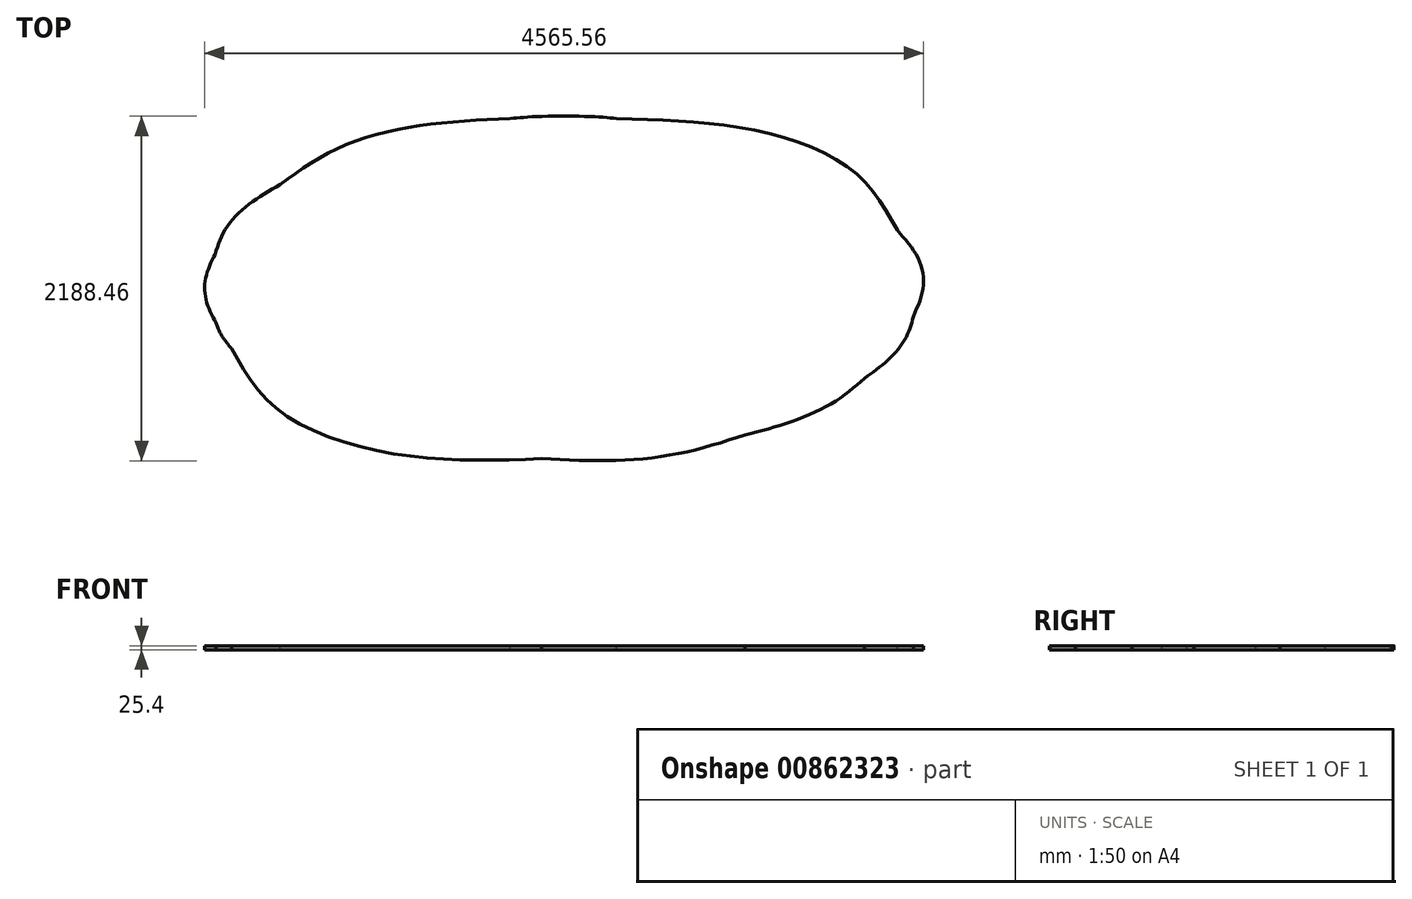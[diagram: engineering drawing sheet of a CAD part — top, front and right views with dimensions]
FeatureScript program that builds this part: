
annotation { "Feature Type Name" : "Feature", "Feature Type Description" : "" }
export const myFeature = defineFeature(function(context is Context, id is Id, definition is map)
    precondition{}
    {
        {
            var Q0;
            Q0=qCreatedBy(makeId("Top.planeOp"),FACE);
            var sketch = newSketch(context, id + "F0", { "sketchPlane" : qUnion([Q0])});
            skLineSegment(sketch, "E0", {"start": v(-77.13, -787.1) * mm, "end": v(-35, -787.1) * mm});
            skLineSegment(sketch, "E1", {"start": v(-35, -787.1) * mm, "end": v(-21.6, -746.82) * mm});
            skLineSegment(sketch, "E2", {"start": v(21.27, -746.77) * mm, "end": v(33.87, -784.57) * mm});
            skLineSegment(sketch, "E3", {"start": v(33.87, -784.57) * mm, "end": v(77.97, -786.03) * mm});
            skLineSegment(sketch, "E4", {"start": v(87.03, -826.55) * mm, "end": v(52.38, -853.41) * mm});
            skLineSegment(sketch, "E5", {"start": v(52.38, -853.41) * mm, "end": v(64.55, -889.18) * mm});
            skLineSegment(sketch, "E6", {"start": v(-79.54, -938.83) * mm, "end": v(-79.54, -938.83) * mm});
            skLineSegment(sketch, "E7", {"start": v(-405.14, -731.65) * mm, "end": v(-373.47, -731.65) * mm});
            skLineSegment(sketch, "E8", {"start": v(-373.47, -731.65) * mm, "end": v(-364.31, -701.4) * mm});
            skLineSegment(sketch, "E9", {"start": v(-330.23, -701.41) * mm, "end": v(-321.34, -731.65) * mm});
            skLineSegment(sketch, "E10", {"start": v(-321.34, -731.65) * mm, "end": v(-288.94, -731.65) * mm});
            skLineSegment(sketch, "E11", {"start": v(-288.47, -772.67) * mm, "end": v(-303.5, -785.97) * mm});
            skLineSegment(sketch, "E12", {"start": v(-303.5, -785.97) * mm, "end": v(-294.85, -813.44) * mm});
            skLineSegment(sketch, "E13", {"start": v(-322.06, -834.55) * mm, "end": v(-346.67, -816.48) * mm});
            skLineSegment(sketch, "E14", {"start": v(-346.67, -816.48) * mm, "end": v(-371.3, -834.55) * mm});
            skLineSegment(sketch, "E15", {"start": v(292.75, -813.28) * mm, "end": v(302.15, -783.08) * mm});
            skLineSegment(sketch, "E16", {"start": v(302.15, -783.08) * mm, "end": v(277.64, -764.38) * mm});
            skLineSegment(sketch, "E17", {"start": v(285.47, -731.65) * mm, "end": v(317.8, -731.65) * mm});
            skLineSegment(sketch, "E18", {"start": v(317.8, -731.65) * mm, "end": v(327.47, -702.67) * mm});
            skLineSegment(sketch, "E19", {"start": v(362.59, -701.06) * mm, "end": v(371.57, -731.64) * mm});
            skLineSegment(sketch, "E20", {"start": v(371.57, -731.64) * mm, "end": v(405.6, -731.64) * mm});
            skLineSegment(sketch, "E21", {"start": v(364.32, -830.54) * mm, "end": v(343.95, -816.03) * mm});
            skLineSegment(sketch, "E22", {"start": v(343.95, -816.03) * mm, "end": v(321.63, -834.33) * mm});
            skLineSegment(sketch, "E23", {"start": v(-1400.1, -366.23) * mm, "end": v(-1400.1, -398.99) * mm});
            skLineSegment(sketch, "E24", {"start": v(-1400.1, -398.99) * mm, "end": v(-1347.18, -398.99) * mm});
            skLineSegment(sketch, "E25", {"start": v(-1347.18, -398.99) * mm, "end": v(-1294.25, -398.99) * mm});
            skLineSegment(sketch, "E26", {"start": v(-1294.25, -398.99) * mm, "end": v(-1294.25, -369.56) * mm});
            skLineSegment(sketch, "E27", {"start": v(-1294.25, -458.02) * mm, "end": v(-1294.25, -429.23) * mm});
            skLineSegment(sketch, "E28", {"start": v(-1294.25, -429.23) * mm, "end": v(-1347.18, -429.23) * mm});
            skLineSegment(sketch, "E29", {"start": v(-1347.18, -429.23) * mm, "end": v(-1400.1, -429.23) * mm});
            skLineSegment(sketch, "E30", {"start": v(-1400.1, -429.23) * mm, "end": v(-1400.1, -461.65) * mm});
            skLineSegment(sketch, "E31", {"start": v(-1121.42, -405.3) * mm, "end": v(-1083.64, -310.78) * mm});
            skLineSegment(sketch, "E32", {"start": v(-1083.64, -310.78) * mm, "end": v(-1062.94, -309.23) * mm});
            skLineSegment(sketch, "E33", {"start": v(-1063.2, -465.59) * mm, "end": v(-1106.64, -464.14) * mm});
            skLineSegment(sketch, "E34", {"start": v(-1106.64, -464.14) * mm, "end": v(-1111.77, -478.84) * mm});
            skLineSegment(sketch, "E35", {"start": v(-823.63, -524) * mm, "end": v(-839.34, -525.54) * mm});
            skLineSegment(sketch, "E36", {"start": v(-839.34, -525.54) * mm, "end": v(-875.93, -434.22) * mm});
            skLineSegment(sketch, "E37", {"start": v(-571.43, -308.26) * mm, "end": v(-493.78, -308.26) * mm});
            skLineSegment(sketch, "E38", {"start": v(-493.78, -308.26) * mm, "end": v(-492.05, -336.47) * mm});
            skLineSegment(sketch, "E39", {"start": v(-553.33, -338.5) * mm, "end": v(-588.6, -338.5) * mm});
            skLineSegment(sketch, "E40", {"start": v(-588.6, -338.5) * mm, "end": v(-588.6, -368.75) * mm});
            skLineSegment(sketch, "E41", {"start": v(-588.6, -368.75) * mm, "end": v(-588.6, -398.99) * mm});
            skLineSegment(sketch, "E42", {"start": v(-588.6, -398.99) * mm, "end": v(-550.8, -398.99) * mm});
            skLineSegment(sketch, "E43", {"start": v(-550.8, -398.99) * mm, "end": v(-513, -398.99) * mm});
            skLineSegment(sketch, "E44", {"start": v(-513, -398.99) * mm, "end": v(-513, -414.11) * mm});
            skLineSegment(sketch, "E45", {"start": v(-513, -414.11) * mm, "end": v(-513, -429.23) * mm});
            skLineSegment(sketch, "E46", {"start": v(-513, -429.23) * mm, "end": v(-550.8, -429.23) * mm});
            skLineSegment(sketch, "E47", {"start": v(-550.8, -429.23) * mm, "end": v(-588.6, -429.23) * mm});
            skLineSegment(sketch, "E48", {"start": v(-588.6, -429.23) * mm, "end": v(-588.6, -459.47) * mm});
            skLineSegment(sketch, "E49", {"start": v(-588.6, -459.47) * mm, "end": v(-588.6, -489.72) * mm});
            skLineSegment(sketch, "E50", {"start": v(-588.6, -489.72) * mm, "end": v(-553.68, -489.72) * mm});
            skLineSegment(sketch, "E51", {"start": v(-492.84, -499.8) * mm, "end": v(-492.84, -525) * mm});
            skLineSegment(sketch, "E52", {"start": v(-492.84, -525) * mm, "end": v(-570.97, -525) * mm});
            skLineSegment(sketch, "E53", {"start": v(-570.97, -525) * mm, "end": v(-649.1, -525) * mm});
            skLineSegment(sketch, "E54", {"start": v(-649.1, -525) * mm, "end": v(-649.1, -512.74) * mm});
            skLineSegment(sketch, "E55", {"start": v(-211.35, -443.08) * mm, "end": v(-240.83, -445.75) * mm});
            skLineSegment(sketch, "E56", {"start": v(-240.83, -445.75) * mm, "end": v(-240.83, -469.04) * mm});
            skLineSegment(sketch, "E57", {"start": v(-215.8, -339.63) * mm, "end": v(-240.83, -337.22) * mm});
            skLineSegment(sketch, "E58", {"start": v(-240.83, -337.22) * mm, "end": v(-240.83, -375.67) * mm});
            skLineSegment(sketch, "E59", {"start": v(-240.83, -375.67) * mm, "end": v(-240.83, -414.11) * mm});
            skLineSegment(sketch, "E60", {"start": v(-240.83, -414.11) * mm, "end": v(-218.15, -414.11) * mm});
            skLineSegment(sketch, "E61", {"start": v(11.02, -339.63) * mm, "end": v(-14.01, -337.22) * mm});
            skLineSegment(sketch, "E62", {"start": v(-14.01, -337.22) * mm, "end": v(-14.01, -369.79) * mm});
            skLineSegment(sketch, "E63", {"start": v(527.2, -338.5) * mm, "end": v(505.14, -338.5) * mm});
            skLineSegment(sketch, "E64", {"start": v(505.14, -338.5) * mm, "end": v(505.14, -414.11) * mm});
            skLineSegment(sketch, "E65", {"start": v(505.14, -414.11) * mm, "end": v(505.14, -489.72) * mm});
            skLineSegment(sketch, "E66", {"start": v(505.14, -489.72) * mm, "end": v(540.93, -489.72) * mm});
            skLineSegment(sketch, "E67", {"start": v(1149.04, -312.65) * mm, "end": v(1170.46, -318.73) * mm});
            skLineSegment(sketch, "E68", {"start": v(1170.46, -318.73) * mm, "end": v(1170.46, -348.78) * mm});
            skLineSegment(sketch, "E69", {"start": v(1306.55, -416.04) * mm, "end": v(1306.55, -338.5) * mm});
            skLineSegment(sketch, "E70", {"start": v(1306.55, -338.5) * mm, "end": v(1287.58, -338.5) * mm});
            skLineSegment(sketch, "E71", {"start": v(1235.98, -336.34) * mm, "end": v(1235.98, -308.26) * mm});
            skLineSegment(sketch, "E72", {"start": v(1235.98, -308.26) * mm, "end": v(1324.19, -308.26) * mm});
            skLineSegment(sketch, "E73", {"start": v(1324.19, -308.26) * mm, "end": v(1412.4, -308.26) * mm});
            skLineSegment(sketch, "E74", {"start": v(1412.4, -308.26) * mm, "end": v(1412.4, -335.99) * mm});
            skLineSegment(sketch, "E75", {"start": v(1361.18, -338.5) * mm, "end": v(1341.83, -338.5) * mm});
            skLineSegment(sketch, "E76", {"start": v(1341.83, -338.5) * mm, "end": v(1341.83, -416.04) * mm});
            skLineSegment(sketch, "E77", {"start": v(-203.24, -62.83) * mm, "end": v(-203.03, -82) * mm});
            skLineSegment(sketch, "E78", {"start": v(-203.03, -82) * mm, "end": v(-192.57, -68.9) * mm});
            skLineSegment(sketch, "E79", {"start": v(-258.67, -83) * mm, "end": v(-264.15, -71.95) * mm});
            skLineSegment(sketch, "E80", {"start": v(-264.15, -71.95) * mm, "end": v(-278.95, -81.83) * mm});
            skLineSegment(sketch, "E81", {"start": v(-221.68, -47.39) * mm, "end": v(-223.24, -23.49) * mm});
            skLineSegment(sketch, "E82", {"start": v(-223.24, -23.49) * mm, "end": v(-232.38, -41.15) * mm});
            skLineSegment(sketch, "E83", {"start": v(395.88, 11.8) * mm, "end": v(384.78, -8.37) * mm});
            skLineSegment(sketch, "E84", {"start": v(384.78, -8.37) * mm, "end": v(407.82, -8.37) * mm});
            skLineSegment(sketch, "E85", {"start": v(-1447.8, 21.75) * mm, "end": v(-1377.42, 59.43) * mm});
            skLineSegment(sketch, "E86", {"start": v(-1377.42, 59.43) * mm, "end": v(-1368.7, 48.21) * mm});
            skLineSegment(sketch, "E87", {"start": v(1487.2, -38.48) * mm, "end": v(1473.78, -31.2) * mm});
            skLineSegment(sketch, "E88", {"start": v(1473.78, -31.2) * mm, "end": v(1490.32, 30.62) * mm});
            skLineSegment(sketch, "E89", {"start": v(1453.27, 169.57) * mm, "end": v(1395.87, 199.88) * mm});
            skLineSegment(sketch, "E90", {"start": v(1395.87, 199.88) * mm, "end": v(1343.8, 137.73) * mm});
            skLineSegment(sketch, "E91", {"start": v(-1085.78, 301.94) * mm, "end": v(-961.5, 198.93) * mm});
            skLineSegment(sketch, "E92", {"start": v(-961.5, 198.93) * mm, "end": v(-977.92, 191.96) * mm});
            skLineSegment(sketch, "E93", {"start": v(-1234.5, 332.29) * mm, "end": v(-1241.98, 297.43) * mm});
            skLineSegment(sketch, "E94", {"start": v(-1241.98, 297.43) * mm, "end": v(-1207.8, 207.8) * mm});
            skLineSegment(sketch, "E95", {"start": v(1078.67, 153.44) * mm, "end": v(1065.04, 160.58) * mm});
            skLineSegment(sketch, "E96", {"start": v(1065.04, 160.58) * mm, "end": v(1081.73, 199.6) * mm});
            skLineSegment(sketch, "E97", {"start": v(1426.3, 521.33) * mm, "end": v(1428.93, 554) * mm});
            skLineSegment(sketch, "E98", {"start": v(1428.93, 554) * mm, "end": v(1406.64, 575.24) * mm});
            skLineSegment(sketch, "E99", {"start": v(-731.9, 278.38) * mm, "end": v(-728.9, 263.44) * mm});
            skLineSegment(sketch, "E100", {"start": v(-728.9, 263.44) * mm, "end": v(-824.46, 237.16) * mm});
            skLineSegment(sketch, "E101", {"start": v(-412.2, 560.5) * mm, "end": v(-412.2, 577.45) * mm});
            skLineSegment(sketch, "E102", {"start": v(-412.2, 577.45) * mm, "end": v(-358.01, 583.3) * mm});
            skLineSegment(sketch, "E103", {"start": v(192.8, 428.33) * mm, "end": v(166.65, 345.87) * mm});
            skLineSegment(sketch, "E104", {"start": v(166.65, 345.87) * mm, "end": v(151.03, 349) * mm});
            skLineSegment(sketch, "E105", {"start": v(-175.3, 829.59) * mm, "end": v(-175.3, 911.5) * mm});
            skLineSegment(sketch, "E106", {"start": v(-175.3, 911.5) * mm, "end": v(-103.48, 911.46) * mm});
            skLineSegment(sketch, "E107", {"start": v(26.51, 640.04) * mm, "end": v(6.7, 625.7) * mm});
            skLineSegment(sketch, "E108", {"start": v(6.7, 625.7) * mm, "end": v(25.48, 607.36) * mm});
            skLineSegment(sketch, "E109", {"start": v(65.47, 446.52) * mm, "end": v(67.58, 352.02) * mm});
            skLineSegment(sketch, "E110", {"start": v(67.58, 352.02) * mm, "end": v(49.46, 352.02) * mm});
            skLineSegment(sketch, "E111", {"start": v(49.46, 352.02) * mm, "end": v(31.35, 352.02) * mm});
            skLineSegment(sketch, "E112", {"start": v(31.35, 352.02) * mm, "end": v(31.35, 437.53) * mm});
            skLineSegment(sketch, "E113", {"start": v(-97.89, 608.03) * mm, "end": v(-137.5, 606.55) * mm});
            skLineSegment(sketch, "E114", {"start": v(-137.5, 606.55) * mm, "end": v(-135.57, 479.28) * mm});
            skLineSegment(sketch, "E115", {"start": v(-80.8, 875.33) * mm, "end": v(-140.02, 877.27) * mm});
            skLineSegment(sketch, "E116", {"start": v(-140.02, 877.27) * mm, "end": v(-140.02, 760.27) * mm});
            skLineSegment(sketch, "E117", {"start": v(-140.02, 760.27) * mm, "end": v(-140.02, 643.27) * mm});
            skLineSegment(sketch, "E118", {"start": v(-140.02, 643.27) * mm, "end": v(-83.32, 645.1) * mm});
            skFitSpline(sketch, "E119", {"points": [v(-137.5, -1083.85) * mm, v(-1015.8, -1061.97) * mm, v(-1795.97, -784.8) * mm, v(-2107.84, -383.87) * mm]});
            skFitSpline(sketch, "E120", {"points": [v(-2107.84, -383.87) * mm, v(-2158.8, -318.36) * mm, v(-2179.7, -283.92) * mm, v(-2205.75, -222.58) * mm]});
            skFitSpline(sketch, "E121", {"points": [v(-2205.75, -222.58) * mm, v(-2267.88, -76.26) * mm, v(-2269.76, 70.75) * mm, v(-2211.35, 214.41) * mm]});
            skFitSpline(sketch, "E122", {"points": [v(-2211.35, 214.41) * mm, v(-2147.67, 371.03) * mm, v(-2000.3, 528.9) * mm, v(-1798.84, 656.33) * mm]});
            skFitSpline(sketch, "E123", {"points": [v(-1798.84, 656.33) * mm, v(-1440.14, 883.22) * mm, v(-932.63, 1028.95) * mm, v(-336.6, 1076.21) * mm]});
            skFitSpline(sketch, "E124", {"points": [v(-336.6, 1076.21) * mm, v(-184.04, 1088.31) * mm, v(187.36, 1088.34) * mm, v(338.8, 1076.26) * mm]});
            skFitSpline(sketch, "E125", {"points": [v(338.8, 1076.26) * mm, v(1177.61, 1009.38) * mm, v(1835.7, 747.59) * mm, v(2121.4, 367.14) * mm]});
            skFitSpline(sketch, "E126", {"points": [v(2121.4, 367.14) * mm, v(2251.55, 193.84) * mm, v(2286.19, 7.97) * mm, v(2223.32, -179.71) * mm]});
            skFitSpline(sketch, "E127", {"points": [v(2223.32, -179.71) * mm, v(2179.67, -310.03) * mm, v(2067.7, -452.62) * mm, v(1913.9, -573.78) * mm]});
            skFitSpline(sketch, "E128", {"points": [v(1913.9, -573.78) * mm, v(1736.48, -713.56) * mm, v(1454.38, -846.93) * mm, v(1154.15, -932.98) * mm]});
            skFitSpline(sketch, "E129", {"points": [v(1154.15, -932.98) * mm, v(763.99, -1044.82) * mm, v(330.04, -1095.5) * mm, v(-137.5, -1083.85) * mm]});
            skFitSpline(sketch, "E130", {"points": [v(316.13, -1031.21) * mm, v(1052.29, -981.6) * mm, v(1688.5, -757.08) * mm, v(2002.78, -436) * mm]});
            skFitSpline(sketch, "E131", {"points": [v(2002.78, -436) * mm, v(2138.98, -296.83) * mm, v(2201.56, -168.42) * mm, v(2207.48, -15.93) * mm]});
            skFitSpline(sketch, "E132", {"points": [v(2207.48, -15.93) * mm, v(2212.48, 112.6) * mm, v(2176.16, 220.91) * mm, v(2088.34, 339.42) * mm]});
            skFitSpline(sketch, "E133", {"points": [v(2088.34, 339.42) * mm, v(1844.33, 668.69) * mm, v(1269.97, 920.21) * mm, v(558.06, 1009.56) * mm]});
            skFitSpline(sketch, "E134", {"points": [v(558.06, 1009.56) * mm, v(357.95, 1034.68) * mm, v(264.48, 1039.72) * mm, v(-1.41, 1039.72) * mm]});
            skFitSpline(sketch, "E135", {"points": [v(-1.41, 1039.72) * mm, v(-267.35, 1039.72) * mm, v(-360.9, 1034.67) * mm, v(-560.89, 1009.55) * mm]});
            skFitSpline(sketch, "E136", {"points": [v(-560.89, 1009.55) * mm, v(-1048.87, 948.26) * mm, v(-1476.02, 811.35) * mm, v(-1775.6, 620.21) * mm]});
            skFitSpline(sketch, "E137", {"points": [v(-1775.6, 620.21) * mm, v(-1943.91, 512.83) * mm, v(-2088.1, 366.3) * mm, v(-2151.1, 238.6) * mm]});
            skFitSpline(sketch, "E138", {"points": [v(-2151.1, 238.6) * mm, v(-2282.02, -26.7) * mm, v(-2192.45, -299.78) * mm, v(-1899.1, -529.75) * mm]});
            skFitSpline(sketch, "E139", {"points": [v(-1899.1, -529.75) * mm, v(-1432.21, -895.73) * mm, v(-569.94, -1090.93) * mm, v(316.13, -1031.21) * mm]});
            skFitSpline(sketch, "E140", {"points": [v(-79.54, -938.83) * mm, v(-79.54, -935.12) * mm, v(-64.49, -882.35) * mm, v(-56.76, -858.99) * mm]});
            skFitSpline(sketch, "E141", {"points": [v(-56.76, -858.99) * mm, v(-55.63, -855.56) * mm, v(-70.55, -840.11) * mm, v(-89.91, -824.66) * mm]});
            skFitSpline(sketch, "E142", {"points": [v(-89.91, -824.66) * mm, v(-109.28, -809.21) * mm, v(-123.8, -794.44) * mm, v(-122.2, -791.83) * mm]});
            skFitSpline(sketch, "E143", {"points": [v(-122.2, -791.83) * mm, v(-120.58, -789.23) * mm, v(-100.3, -787.1) * mm, v(-77.13, -787.1) * mm]});
            skFitSpline(sketch, "E144", {"points": [v(-21.6, -746.82) * mm, v(-2.33, -688.98) * mm, v(2, -688.98) * mm, v(21.27, -746.77) * mm]});
            skFitSpline(sketch, "E145", {"points": [v(77.97, -786.03) * mm, v(108.48, -787.03) * mm, v(122.01, -789.36) * mm, v(121.88, -793.59) * mm]});
            skFitSpline(sketch, "E146", {"points": [v(121.88, -793.59) * mm, v(121.76, -796.94) * mm, v(106.09, -811.78) * mm, v(87.03, -826.55) * mm]});
            skFitSpline(sketch, "E147", {"points": [v(64.55, -889.18) * mm, v(77.79, -928.1) * mm, v(79.69, -943.34) * mm, v(71.32, -943.34) * mm]});
            skFitSpline(sketch, "E148", {"points": [v(71.32, -943.34) * mm, v(68.35, -943.34) * mm, v(51.61, -933.13) * mm, v(34.13, -920.66) * mm]});
            skFitSpline(sketch, "E149", {"points": [v(34.13, -920.66) * mm, v(16.65, -908.18) * mm, v(0.76, -897.98) * mm, v(-1.18, -897.98) * mm]});
            skFitSpline(sketch, "E150", {"points": [v(-1.18, -897.98) * mm, v(-3.11, -897.98) * mm, v(-17.96, -908.18) * mm, v(-34.17, -920.66) * mm]});
            skFitSpline(sketch, "E151", {"points": [v(-34.17, -920.66) * mm, v(-61.91, -942) * mm, v(-79.54, -949.06) * mm, v(-79.54, -938.83) * mm]});
            skFitSpline(sketch, "E152", {"points": [v(-407.16, -843.44) * mm, v(-407.16, -838.38) * mm, v(-403.41, -823.25) * mm, v(-398.83, -809.81) * mm]});
            skFitSpline(sketch, "E153", {"points": [v(-398.83, -809.81) * mm, v(-389.59, -782.69) * mm, v(-389.46, -782.92) * mm, v(-429.44, -753.83) * mm]});
            skFitSpline(sketch, "E154", {"points": [v(-429.44, -753.83) * mm, v(-450.19, -738.73) * mm, v(-442.43, -731.65) * mm, v(-405.14, -731.65) * mm]});
            skFitSpline(sketch, "E155", {"points": [v(-364.31, -701.4) * mm, v(-352.1, -661.07) * mm, v(-342.08, -661.08) * mm, v(-330.23, -701.41) * mm]});
            skFitSpline(sketch, "E156", {"points": [v(-288.94, -731.65) * mm, v(-252.53, -731.65) * mm, v(-242.25, -739.02) * mm, v(-261.31, -751.46) * mm]});
            skFitSpline(sketch, "E157", {"points": [v(-261.31, -751.46) * mm, v(-267.98, -755.81) * mm, v(-280.2, -765.36) * mm, v(-288.47, -772.67) * mm]});
            skFitSpline(sketch, "E158", {"points": [v(-294.85, -813.44) * mm, v(-280.26, -859.72) * mm, v(-283.9, -862.55) * mm, v(-322.06, -834.55) * mm]});
            skFitSpline(sketch, "E159", {"points": [v(-371.3, -834.55) * mm, v(-398.9, -854.81) * mm, v(-407.16, -856.86) * mm, v(-407.16, -843.44) * mm]});
            skFitSpline(sketch, "E160", {"points": [v(286.18, -848.05) * mm, v(284.62, -845.53) * mm, v(287.58, -829.89) * mm, v(292.75, -813.28) * mm]});
            skFitSpline(sketch, "E161", {"points": [v(277.64, -764.38) * mm, v(243.59, -738.41) * mm, v(245.2, -731.65) * mm, v(285.47, -731.65) * mm]});
            skFitSpline(sketch, "E162", {"points": [v(327.47, -702.67) * mm, v(340.92, -662.3) * mm, v(351.06, -661.84) * mm, v(362.59, -701.06) * mm]});
            skFitSpline(sketch, "E163", {"points": [v(405.6, -731.64) * mm, v(447.89, -731.65) * mm, v(449.73, -738.49) * mm, v(414.41, -764.41) * mm]});
            skFitSpline(sketch, "E164", {"points": [v(414.41, -764.41) * mm, v(400.55, -774.59) * mm, v(389.21, -783.5) * mm, v(389.21, -784.21) * mm]});
            skFitSpline(sketch, "E165", {"points": [v(389.21, -784.21) * mm, v(389.21, -784.93) * mm, v(393.77, -798.77) * mm, v(399.35, -814.98) * mm]});
            skFitSpline(sketch, "E166", {"points": [v(399.35, -814.98) * mm, v(409.93, -845.73) * mm, v(406.82, -860.28) * mm, v(391.85, -849.98) * mm]});
            skFitSpline(sketch, "E167", {"points": [v(391.85, -849.98) * mm, v(387.91, -847.27) * mm, v(375.52, -838.53) * mm, v(364.32, -830.54) * mm]});
            skFitSpline(sketch, "E168", {"points": [v(321.63, -834.33) * mm, v(298.73, -853.09) * mm, v(291.11, -856.04) * mm, v(286.18, -848.05) * mm]});
            skFitSpline(sketch, "E169", {"points": [v(-1645.81, -519.36) * mm, v(-1661.96, -514.7) * mm, v(-1662.2, -514.2) * mm, v(-1662.2, -484.2) * mm]});
            skFitSpline(sketch, "E170", {"points": [v(-1662.2, -484.2) * mm, v(-1662.2, -453.98) * mm, v(-1662.1, -453.77) * mm, v(-1648.36, -455.36) * mm]});
            skFitSpline(sketch, "E171", {"points": [v(-1648.36, -455.36) * mm, v(-1637.42, -456.62) * mm, v(-1633.98, -460.12) * mm, v(-1631.94, -472.07) * mm]});
            skFitSpline(sketch, "E172", {"points": [v(-1631.94, -472.07) * mm, v(-1629.81, -484.55) * mm, v(-1626.08, -488) * mm, v(-1610.61, -491.84) * mm]});
            skFitSpline(sketch, "E173", {"points": [v(-1610.61, -491.84) * mm, v(-1565.6, -502.98) * mm, v(-1537.16, -454.37) * mm, v(-1578.47, -436.89) * mm]});
            skFitSpline(sketch, "E174", {"points": [v(-1578.47, -436.89) * mm, v(-1587.1, -433.24) * mm, v(-1604.13, -426.12) * mm, v(-1616.32, -421.08) * mm]});
            skFitSpline(sketch, "E175", {"points": [v(-1616.32, -421.08) * mm, v(-1665.18, -400.86) * mm, v(-1671.5, -344.35) * mm, v(-1627.93, -317.42) * mm]});
            skFitSpline(sketch, "E176", {"points": [v(-1627.93, -317.42) * mm, v(-1614.5, -309.1) * mm, v(-1603.68, -306.9) * mm, v(-1580.5, -307.74) * mm]});
            skFitSpline(sketch, "E177", {"points": [v(-1580.5, -307.74) * mm, v(-1531.22, -309.52) * mm, v(-1526.1, -313.14) * mm, v(-1526.1, -346.28) * mm]});
            skFitSpline(sketch, "E178", {"points": [v(-1526.1, -346.28) * mm, v(-1526.1, -374.03) * mm, v(-1526.31, -374.43) * mm, v(-1539.94, -372.86) * mm]});
            skFitSpline(sketch, "E179", {"points": [v(-1539.94, -372.86) * mm, v(-1550.89, -371.6) * mm, v(-1554.32, -368.1) * mm, v(-1556.35, -356.15) * mm]});
            skFitSpline(sketch, "E180", {"points": [v(-1556.35, -356.15) * mm, v(-1558.72, -342.18) * mm, v(-1560.7, -340.91) * mm, v(-1582.23, -339.51) * mm]});
            skFitSpline(sketch, "E181", {"points": [v(-1582.23, -339.51) * mm, v(-1607.26, -337.9) * mm, v(-1621.87, -346.65) * mm, v(-1621.87, -363.29) * mm]});
            skFitSpline(sketch, "E182", {"points": [v(-1621.87, -363.29) * mm, v(-1621.87, -375.63) * mm, v(-1609.16, -385.34) * mm, v(-1575.65, -398.6) * mm]});
            skFitSpline(sketch, "E183", {"points": [v(-1575.65, -398.6) * mm, v(-1542.65, -411.67) * mm, v(-1533.97, -419.9) * mm, v(-1527.43, -444.35) * mm]});
            skFitSpline(sketch, "E184", {"points": [v(-1527.43, -444.35) * mm, v(-1512.04, -501.94) * mm, v(-1572.81, -540.44) * mm, v(-1645.81, -519.36) * mm]});
            skFitSpline(sketch, "E185", {"points": [v(-1455.54, -512.8) * mm, v(-1455.54, -505.3) * mm, v(-1451.43, -497.95) * mm, v(-1445.46, -494.76) * mm]});
            skFitSpline(sketch, "E186", {"points": [v(-1445.46, -494.76) * mm, v(-1436.07, -489.73) * mm, v(-1435.38, -484.2) * mm, v(-1435.38, -413.46) * mm]});
            skFitSpline(sketch, "E187", {"points": [v(-1435.38, -413.46) * mm, v(-1435.38, -341.8) * mm, v(-1435.94, -337.41) * mm, v(-1445.46, -334.93) * mm]});
            skFitSpline(sketch, "E188", {"points": [v(-1445.46, -334.93) * mm, v(-1451.99, -333.22) * mm, v(-1455.54, -328.05) * mm, v(-1455.54, -320.28) * mm]});
            skFitSpline(sketch, "E189", {"points": [v(-1455.54, -320.28) * mm, v(-1455.54, -308.69) * mm, v(-1454.2, -308.26) * mm, v(-1417.74, -308.26) * mm]});
            skFitSpline(sketch, "E190", {"points": [v(-1417.74, -308.26) * mm, v(-1380.78, -308.26) * mm, v(-1379.94, -308.54) * mm, v(-1379.94, -320.86) * mm]});
            skFitSpline(sketch, "E191", {"points": [v(-1379.94, -320.86) * mm, v(-1379.94, -330.1) * mm, v(-1382.63, -333.47) * mm, v(-1390.02, -333.47) * mm]});
            skFitSpline(sketch, "E192", {"points": [v(-1390.02, -333.47) * mm, v(-1399.07, -333.47) * mm, v(-1400.1, -336.83) * mm, v(-1400.1, -366.23) * mm]});
            skFitSpline(sketch, "E193", {"points": [v(-1294.25, -369.56) * mm, v(-1294.25, -343.82) * mm, v(-1295.7, -339.47) * mm, v(-1305.73, -334.9) * mm]});
            skFitSpline(sketch, "E194", {"points": [v(-1305.73, -334.9) * mm, v(-1312.05, -332.02) * mm, v(-1317.58, -324.85) * mm, v(-1318.02, -318.96) * mm]});
            skFitSpline(sketch, "E195", {"points": [v(-1318.02, -318.96) * mm, v(-1318.78, -308.89) * mm, v(-1316.5, -308.26) * mm, v(-1278.82, -308.26) * mm]});
            skFitSpline(sketch, "E196", {"points": [v(-1278.82, -308.26) * mm, v(-1241.57, -308.26) * mm, v(-1238.8, -309) * mm, v(-1238.8, -318.82) * mm]});
            skFitSpline(sketch, "E197", {"points": [v(-1238.8, -318.82) * mm, v(-1238.8, -325.13) * mm, v(-1242.86, -330.43) * mm, v(-1248.89, -332) * mm]});
            skFitSpline(sketch, "E198", {"points": [v(-1248.89, -332) * mm, v(-1258.43, -334.5) * mm, v(-1258.97, -338.88) * mm, v(-1258.97, -414.11) * mm]});
            skFitSpline(sketch, "E199", {"points": [v(-1258.97, -414.11) * mm, v(-1258.97, -489.34) * mm, v(-1258.43, -493.72) * mm, v(-1248.89, -496.22) * mm]});
            skFitSpline(sketch, "E200", {"points": [v(-1248.89, -496.22) * mm, v(-1242.08, -498) * mm, v(-1238.8, -503.1) * mm, v(-1238.8, -511.92) * mm]});
            skFitSpline(sketch, "E201", {"points": [v(-1238.8, -511.92) * mm, v(-1238.8, -524.82) * mm, v(-1239.33, -525) * mm, v(-1276.07, -525) * mm]});
            skFitSpline(sketch, "E202", {"points": [v(-1276.07, -525) * mm, v(-1306.87, -525) * mm, v(-1313.92, -523.47) * mm, v(-1316.7, -516.2) * mm]});
            skFitSpline(sketch, "E203", {"points": [v(-1316.7, -516.2) * mm, v(-1319.02, -510.19) * mm, v(-1316, -504.16) * mm, v(-1307.17, -497.11) * mm]});
            skFitSpline(sketch, "E204", {"points": [v(-1307.17, -497.11) * mm, v(-1296.02, -488.22) * mm, v(-1294.25, -482.88) * mm, v(-1294.25, -458.02) * mm]});
            skFitSpline(sketch, "E205", {"points": [v(-1400.1, -461.65) * mm, v(-1400.1, -489.96) * mm, v(-1398.78, -494.5) * mm, v(-1389.72, -497.37) * mm]});
            skFitSpline(sketch, "E206", {"points": [v(-1389.72, -497.37) * mm, v(-1382.68, -499.6) * mm, v(-1379.85, -504.16) * mm, v(-1380.9, -511.57) * mm]});
            skFitSpline(sketch, "E207", {"points": [v(-1380.9, -511.57) * mm, v(-1382.31, -521.44) * mm, v(-1385.92, -522.62) * mm, v(-1419, -523.96) * mm]});
            skFitSpline(sketch, "E208", {"points": [v(-1419, -523.96) * mm, v(-1455.05, -525.42) * mm, v(-1455.54, -525.27) * mm, v(-1455.54, -512.8) * mm]});
            skFitSpline(sketch, "E209", {"points": [v(-1169.92, -521.64) * mm, v(-1176.05, -515.5) * mm, v(-1173.4, -499.8) * mm, v(-1166.24, -499.8) * mm]});
            skFitSpline(sketch, "E210", {"points": [v(-1166.24, -499.8) * mm, v(-1161.8, -499.8) * mm, v(-1145.22, -464.83) * mm, v(-1121.42, -405.3) * mm]});
            skFitSpline(sketch, "E211", {"points": [v(-1062.94, -309.23) * mm, v(-1048.24, -308.13) * mm, v(-1042.24, -309.64) * mm, v(-1042.24, -314.43) * mm]});
            skFitSpline(sketch, "E212", {"points": [v(-1042.24, -314.43) * mm, v(-1042.24, -328.69) * mm, v(-975.66, -487.62) * mm, v(-966.35, -495.56) * mm]});
            skFitSpline(sketch, "E213", {"points": [v(-966.35, -495.56) * mm, v(-960.96, -500.17) * mm, v(-956.55, -508.67) * mm, v(-956.55, -514.46) * mm]});
            skFitSpline(sketch, "E214", {"points": [v(-956.55, -514.46) * mm, v(-956.55, -524.07) * mm, v(-959.44, -525) * mm, v(-989.31, -525) * mm]});
            skFitSpline(sketch, "E215", {"points": [v(-989.31, -525) * mm, v(-1020.6, -525) * mm, v(-1022.08, -524.45) * mm, v(-1022.08, -512.82) * mm]});
            skFitSpline(sketch, "E216", {"points": [v(-1022.08, -512.82) * mm, v(-1022.08, -506.12) * mm, v(-1019.24, -499.69) * mm, v(-1015.78, -498.53) * mm]});
            skFitSpline(sketch, "E217", {"points": [v(-1015.78, -498.53) * mm, v(-1011.05, -496.96) * mm, v(-1010.76, -492.76) * mm, v(-1014.62, -481.73) * mm]});
            skFitSpline(sketch, "E218", {"points": [v(-1014.62, -481.73) * mm, v(-1019.71, -467.2) * mm, v(-1020.27, -467.02) * mm, v(-1063.2, -465.59) * mm]});
            skFitSpline(sketch, "E219", {"points": [v(-1111.77, -478.84) * mm, v(-1115.8, -490.4) * mm, v(-1115.23, -495.2) * mm, v(-1109.12, -501.32) * mm]});
            skFitSpline(sketch, "E220", {"points": [v(-1109.12, -501.32) * mm, v(-1094.34, -516.1) * mm, v(-1104.83, -525) * mm, v(-1137, -525) * mm]});
            skFitSpline(sketch, "E221", {"points": [v(-1137, -525) * mm, v(-1153.26, -525) * mm, v(-1168.08, -523.49) * mm, v(-1169.92, -521.64) * mm]});
            skFitSpline(sketch, "E222", {"points": [v(-1037.2, -427.97) * mm, v(-1037.2, -419.79) * mm, v(-1056.96, -367.43) * mm, v(-1062.02, -362.2) * mm]});
            skFitSpline(sketch, "E223", {"points": [v(-1062.02, -362.2) * mm, v(-1064.16, -360) * mm, v(-1071.1, -372.47) * mm, v(-1077.44, -389.93) * mm]});
            skFitSpline(sketch, "E224", {"points": [v(-1077.44, -389.93) * mm, v(-1083.78, -407.39) * mm, v(-1090.04, -424.5) * mm, v(-1091.35, -427.97) * mm]});
            skFitSpline(sketch, "E225", {"points": [v(-1091.35, -427.97) * mm, v(-1093.07, -432.54) * mm, v(-1085.97, -434.27) * mm, v(-1065.46, -434.27) * mm]});
            skFitSpline(sketch, "E226", {"points": [v(-1065.46, -434.27) * mm, v(-1046.2, -434.27) * mm, v(-1037.2, -432.26) * mm, v(-1037.2, -427.97) * mm]});
            skFitSpline(sketch, "E227", {"points": [v(-875.93, -434.22) * mm, v(-902.13, -368.83) * mm, v(-915.9, -340.69) * mm, v(-924.45, -335.09) * mm]});
            skFitSpline(sketch, "E228", {"points": [v(-924.45, -335.09) * mm, v(-931.02, -330.79) * mm, v(-936.4, -323) * mm, v(-936.4, -317.76) * mm]});
            skFitSpline(sketch, "E229", {"points": [v(-936.4, -317.76) * mm, v(-936.4, -309.3) * mm, v(-932.26, -308.26) * mm, v(-898.59, -308.26) * mm]});
            skFitSpline(sketch, "E230", {"points": [v(-898.59, -308.26) * mm, v(-861.63, -308.26) * mm, v(-860.79, -308.54) * mm, v(-860.79, -320.86) * mm]});
            skFitSpline(sketch, "E231", {"points": [v(-860.79, -320.86) * mm, v(-860.79, -328.7) * mm, v(-863.64, -333.47) * mm, v(-868.35, -333.47) * mm]});
            skFitSpline(sketch, "E232", {"points": [v(-868.35, -333.47) * mm, v(-872.5, -333.47) * mm, v(-875.97, -335.17) * mm, v(-876.05, -337.25) * mm]});
            skFitSpline(sketch, "E233", {"points": [v(-876.05, -337.25) * mm, v(-876.3, -344.04) * mm, v(-828.1, -464.49) * mm, v(-825.13, -464.5) * mm]});
            skFitSpline(sketch, "E234", {"points": [v(-825.13, -464.5) * mm, v(-821.61, -464.52) * mm, v(-775.1, -348.47) * mm, v(-775.1, -339.69) * mm]});
            skFitSpline(sketch, "E235", {"points": [v(-775.1, -339.69) * mm, v(-775.1, -336.26) * mm, v(-778.5, -333.47) * mm, v(-782.66, -333.47) * mm]});
            skFitSpline(sketch, "E236", {"points": [v(-782.66, -333.47) * mm, v(-787.37, -333.47) * mm, v(-790.22, -328.7) * mm, v(-790.22, -320.86) * mm]});
            skFitSpline(sketch, "E237", {"points": [v(-790.22, -320.86) * mm, v(-790.22, -308.54) * mm, v(-789.38, -308.26) * mm, v(-752.42, -308.26) * mm]});
            skFitSpline(sketch, "E238", {"points": [v(-752.42, -308.26) * mm, v(-715.76, -308.26) * mm, v(-714.62, -308.63) * mm, v(-714.62, -320.5) * mm]});
            skFitSpline(sketch, "E239", {"points": [v(-714.62, -320.5) * mm, v(-714.62, -327.87) * mm, v(-717.93, -333.37) * mm, v(-722.98, -334.36) * mm]});
            skFitSpline(sketch, "E240", {"points": [v(-722.98, -334.36) * mm, v(-728.58, -335.45) * mm, v(-743.97, -366.74) * mm, v(-769.63, -429.23) * mm]});
            skFitSpline(sketch, "E241", {"points": [v(-769.63, -429.23) * mm, v(-807.07, -520.4) * mm, v(-808.27, -522.51) * mm, v(-823.63, -524) * mm]});
            skFitSpline(sketch, "E242", {"points": [v(-649.1, -512.74) * mm, v(-649.1, -504.9) * mm, v(-645.45, -499.32) * mm, v(-639.01, -497.28) * mm]});
            skFitSpline(sketch, "E243", {"points": [v(-639.01, -497.28) * mm, v(-629.5, -494.26) * mm, v(-628.93, -489.65) * mm, v(-628.93, -416.47) * mm]});
            skFitSpline(sketch, "E244", {"points": [v(-628.93, -416.47) * mm, v(-628.93, -344.02) * mm, v(-629.6, -338.5) * mm, v(-639.01, -333.47) * mm]});
            skFitSpline(sketch, "E245", {"points": [v(-639.01, -333.47) * mm, v(-644.56, -330.5) * mm, v(-649.1, -323.61) * mm, v(-649.1, -318.17) * mm]});
            skFitSpline(sketch, "E246", {"points": [v(-649.1, -318.17) * mm, v(-649.1, -308.75) * mm, v(-645.27, -308.26) * mm, v(-571.43, -308.26) * mm]});
            skFitSpline(sketch, "E247", {"points": [v(-492.05, -336.47) * mm, v(-490.14, -367.59) * mm, v(-491.17, -369.56) * mm, v(-507.09, -365.4) * mm]});
            skFitSpline(sketch, "E248", {"points": [v(-507.09, -365.4) * mm, v(-514.47, -363.47) * mm, v(-518.05, -358.61) * mm, v(-518.05, -350.52) * mm]});
            skFitSpline(sketch, "E249", {"points": [v(-518.05, -350.52) * mm, v(-518.05, -339) * mm, v(-519.51, -338.5) * mm, v(-553.33, -338.5) * mm]});
            skFitSpline(sketch, "E250", {"points": [v(-553.68, -489.72) * mm, v(-521.29, -489.72) * mm, v(-518.63, -488.89) * mm, v(-517.14, -478.37) * mm]});
            skFitSpline(sketch, "E251", {"points": [v(-517.14, -478.37) * mm, v(-516, -470.45) * mm, v(-512.1, -467.03) * mm, v(-504.18, -467.03) * mm]});
            skFitSpline(sketch, "E252", {"points": [v(-504.18, -467.03) * mm, v(-497.95, -467.03) * mm, v(-492.84, -468.74) * mm, v(-492.84, -470.81) * mm]});
            skFitSpline(sketch, "E253", {"points": [v(-492.84, -470.81) * mm, v(-492.84, -472.9) * mm, v(-492.84, -485.94) * mm, v(-492.84, -499.8) * mm]});
            skFitSpline(sketch, "E254", {"points": [v(-298.56, -516.22) * mm, v(-300.76, -510.5) * mm, v(-298.32, -504.52) * mm, v(-291.54, -499.03) * mm]});
            skFitSpline(sketch, "E255", {"points": [v(-291.54, -499.03) * mm, v(-281.85, -491.19) * mm, v(-281.15, -485.32) * mm, v(-281.15, -412.04) * mm]});
            skFitSpline(sketch, "E256", {"points": [v(-281.15, -412.04) * mm, v(-281.15, -348.24) * mm, v(-282.47, -333.47) * mm, v(-288.17, -333.47) * mm]});
            skFitSpline(sketch, "E257", {"points": [v(-288.17, -333.47) * mm, v(-294.78, -333.47) * mm, v(-301.31, -323.23) * mm, v(-301.31, -312.9) * mm]});
            skFitSpline(sketch, "E258", {"points": [v(-301.31, -312.9) * mm, v(-301.31, -304.93) * mm, v(-186.8, -307.28) * mm, v(-170.76, -315.57) * mm]});
            skFitSpline(sketch, "E259", {"points": [v(-170.76, -315.57) * mm, v(-153.25, -324.62) * mm, v(-141.78, -341.63) * mm, v(-137.39, -365.06) * mm]});
            skFitSpline(sketch, "E260", {"points": [v(-137.39, -365.06) * mm, v(-129.48, -407.21) * mm, v(-158.98, -438.33) * mm, v(-211.35, -443.08) * mm]});
            skFitSpline(sketch, "E261", {"points": [v(-240.83, -469.04) * mm, v(-240.83, -486.87) * mm, v(-238.46, -493.8) * mm, v(-230.75, -498.63) * mm]});
            skFitSpline(sketch, "E262", {"points": [v(-230.75, -498.63) * mm, v(-225.2, -502.09) * mm, v(-220.67, -509.44) * mm, v(-220.67, -514.96) * mm]});
            skFitSpline(sketch, "E263", {"points": [v(-220.67, -514.96) * mm, v(-220.67, -524.08) * mm, v(-224.08, -525) * mm, v(-257.93, -525) * mm]});
            skFitSpline(sketch, "E264", {"points": [v(-257.93, -525) * mm, v(-288.7, -525) * mm, v(-295.78, -523.47) * mm, v(-298.56, -516.22) * mm]});
            skFitSpline(sketch, "E265", {"points": [v(-185.38, -404.03) * mm, v(-173.05, -391.7) * mm, v(-171.62, -357.92) * mm, v(-183.03, -348.45) * mm]});
            skFitSpline(sketch, "E266", {"points": [v(-183.03, -348.45) * mm, v(-187.28, -344.92) * mm, v(-202.02, -340.95) * mm, v(-215.8, -339.63) * mm]});
            skFitSpline(sketch, "E267", {"points": [v(-218.15, -414.11) * mm, v(-202.18, -414.11) * mm, v(-192.48, -411.12) * mm, v(-185.38, -404.03) * mm]});
            skFitSpline(sketch, "E268", {"points": [v(-69.46, -512.15) * mm, v(-69.46, -503.1) * mm, v(-66.24, -498.01) * mm, v(-59.38, -496.22) * mm]});
            skFitSpline(sketch, "E269", {"points": [v(-59.38, -496.22) * mm, v(-49.84, -493.72) * mm, v(-49.3, -489.34) * mm, v(-49.3, -415.57) * mm]});
            skFitSpline(sketch, "E270", {"points": [v(-49.3, -415.57) * mm, v(-49.3, -341.8) * mm, v(-49.84, -337.42) * mm, v(-59.38, -334.93) * mm]});
            skFitSpline(sketch, "E271", {"points": [v(-59.38, -334.93) * mm, v(-65.9, -333.22) * mm, v(-69.46, -328.05) * mm, v(-69.46, -320.28) * mm]});
            skFitSpline(sketch, "E272", {"points": [v(-69.46, -320.28) * mm, v(-69.46, -308.36) * mm, v(-69, -308.26) * mm, v(-15.27, -308.27) * mm]});
            skFitSpline(sketch, "E273", {"points": [v(-15.27, -308.27) * mm, v(49.58, -308.28) * mm, v(69.17, -315.61) * mm, v(83.66, -345.3) * mm]});
            skFitSpline(sketch, "E274", {"points": [v(83.66, -345.3) * mm, v(91.82, -362) * mm, v(92.3, -367.46) * mm, v(87.15, -384.66) * mm]});
            skFitSpline(sketch, "E275", {"points": [v(87.15, -384.66) * mm, v(81.5, -403.53) * mm, v(76.25, -410.22) * mm, v(55.23, -425.36) * mm]});
            skFitSpline(sketch, "E276", {"points": [v(55.23, -425.36) * mm, v(46.99, -431.29) * mm, v(47.78, -433.76) * mm, v(66.13, -459.47) * mm]});
            skFitSpline(sketch, "E277", {"points": [v(66.13, -459.47) * mm, v(77.01, -474.72) * mm, v(92.35, -490.78) * mm, v(100.22, -495.17) * mm]});
            skFitSpline(sketch, "E278", {"points": [v(100.22, -495.17) * mm, v(117.96, -505.06) * mm, v(119.37, -521.79) * mm, v(102.66, -524.16) * mm]});
            skFitSpline(sketch, "E279", {"points": [v(102.66, -524.16) * mm, v(79.1, -527.5) * mm, v(68.25, -520.03) * mm, v(41.24, -481.89) * mm]});
            skFitSpline(sketch, "E280", {"points": [v(41.24, -481.89) * mm, v(0.37, -424.17) * mm, v(-14.01, -419.5) * mm, v(-14.01, -463.93) * mm]});
            skFitSpline(sketch, "E281", {"points": [v(-14.01, -463.93) * mm, v(-14.01, -489.72) * mm, v(-12.65, -493.94) * mm, v(-3.53, -496.32) * mm]});
            skFitSpline(sketch, "E282", {"points": [v(-3.53, -496.32) * mm, v(4, -498.3) * mm, v(6.48, -502.35) * mm, v(5.29, -510.77) * mm]});
            skFitSpline(sketch, "E283", {"points": [v(5.29, -510.77) * mm, v(3.75, -521.63) * mm, v(0.97, -522.58) * mm, v(-32.91, -523.96) * mm]});
            skFitSpline(sketch, "E284", {"points": [v(-32.91, -523.96) * mm, v(-69.41, -525.44) * mm, v(-69.46, -525.42) * mm, v(-69.46, -512.15) * mm]});
            skFitSpline(sketch, "E285", {"points": [v(42.56, -395.45) * mm, v(53.59, -385.47) * mm, v(54.33, -357.2) * mm, v(43.78, -348.45) * mm]});
            skFitSpline(sketch, "E286", {"points": [v(43.78, -348.45) * mm, v(39.53, -344.92) * mm, v(24.8, -340.95) * mm, v(11.02, -339.63) * mm]});
            skFitSpline(sketch, "E287", {"points": [v(-14.01, -369.79) * mm, v(-14.01, -387.7) * mm, v(-12.31, -404.06) * mm, v(-10.23, -406.15) * mm]});
            skFitSpline(sketch, "E288", {"points": [v(-10.23, -406.15) * mm, v(-4.4, -412) * mm, v(32.53, -404.52) * mm, v(42.56, -395.45) * mm]});
            skFitSpline(sketch, "E289", {"points": [v(235.48, -519.24) * mm, v(200, -506.15) * mm, v(167.44, -457.19) * mm, v(167.44, -416.9) * mm]});
            skFitSpline(sketch, "E290", {"points": [v(167.44, -416.9) * mm, v(167.44, -335.46) * mm, v(248.63, -284.53) * mm, v(323.9, -318.75) * mm]});
            skFitSpline(sketch, "E291", {"points": [v(323.9, -318.75) * mm, v(340.05, -326.1) * mm, v(351.17, -336.1) * mm, v(361.7, -352.74) * mm]});
            skFitSpline(sketch, "E292", {"points": [v(361.7, -352.74) * mm, v(375.06, -373.86) * mm, v(376.6, -380.5) * mm, v(376.47, -416.63) * mm]});
            skFitSpline(sketch, "E293", {"points": [v(376.47, -416.63) * mm, v(376.33, -452.08) * mm, v(374.65, -459.43) * mm, v(362.52, -477.5) * mm]});
            skFitSpline(sketch, "E294", {"points": [v(362.52, -477.5) * mm, v(354.92, -488.8) * mm, v(339.53, -503.2) * mm, v(328.3, -509.5) * mm]});
            skFitSpline(sketch, "E295", {"points": [v(328.3, -509.5) * mm, v(304.7, -522.77) * mm, v(258.27, -527.64) * mm, v(235.48, -519.24) * mm]});
            skFitSpline(sketch, "E296", {"points": [v(312.24, -481.5) * mm, v(351.16, -457.25) * mm, v(349.7, -367.1) * mm, v(310.09, -349.05) * mm]});
            skFitSpline(sketch, "E297", {"points": [v(310.09, -349.05) * mm, v(271.66, -331.54) * mm, v(232.52, -341.9) * mm, v(216.59, -373.79) * mm]});
            skFitSpline(sketch, "E298", {"points": [v(216.59, -373.79) * mm, v(203.6, -399.78) * mm, v(204.82, -443.56) * mm, v(219.1, -464.62) * mm]});
            skFitSpline(sketch, "E299", {"points": [v(219.1, -464.62) * mm, v(237.73, -492.07) * mm, v(282.31, -500.16) * mm, v(312.24, -481.5) * mm]});
            skFitSpline(sketch, "E300", {"points": [v(448.37, -521.72) * mm, v(444.02, -514.37) * mm, v(454.03, -494.76) * mm, v(462.13, -494.76) * mm]});
            skFitSpline(sketch, "E301", {"points": [v(462.13, -494.76) * mm, v(468.74, -494.76) * mm, v(469.86, -483.43) * mm, v(469.86, -416.5) * mm]});
            skFitSpline(sketch, "E302", {"points": [v(469.86, -416.5) * mm, v(469.86, -338.37) * mm, v(469.84, -338.25) * mm, v(457.66, -333.62) * mm]});
            skFitSpline(sketch, "E303", {"points": [v(457.66, -333.62) * mm, v(450, -330.7) * mm, v(445.96, -325.6) * mm, v(446.8, -319.88) * mm]});
            skFitSpline(sketch, "E304", {"points": [v(446.8, -319.88) * mm, v(447.98, -311.75) * mm, v(454.87, -310.63) * mm, v(511.82, -309.37) * mm]});
            skFitSpline(sketch, "E305", {"points": [v(511.82, -309.37) * mm, v(566.72, -308.16) * mm, v(578.14, -309.31) * mm, v(594.51, -317.73) * mm]});
            skFitSpline(sketch, "E306", {"points": [v(594.51, -317.73) * mm, v(622.8, -332.28) * mm, v(639.43, -352.83) * mm, v(648.54, -384.48) * mm]});
            skFitSpline(sketch, "E307", {"points": [v(648.54, -384.48) * mm, v(663.5, -436.5) * mm, v(641.2, -491.2) * mm, v(596.76, -511.41) * mm]});
            skFitSpline(sketch, "E308", {"points": [v(596.76, -511.41) * mm, v(577.97, -519.96) * mm, v(560.78, -522.53) * mm, v(512.05, -524.07) * mm]});
            skFitSpline(sketch, "E309", {"points": [v(512.05, -524.07) * mm, v(478.42, -525.13) * mm, v(449.77, -524.07) * mm, v(448.37, -521.72) * mm]});
            skFitSpline(sketch, "E310", {"points": [v(593.21, -473.21) * mm, v(621.93, -444.5) * mm, v(623.2, -386.78) * mm, v(595.71, -359.3) * mm]});
            skFitSpline(sketch, "E311", {"points": [v(595.71, -359.3) * mm, v(580.35, -343.93) * mm, v(562.47, -338.5) * mm, v(527.2, -338.5) * mm]});
            skFitSpline(sketch, "E312", {"points": [v(540.93, -489.72) * mm, v(574.63, -489.72) * mm, v(577.67, -488.76) * mm, v(593.21, -473.21) * mm]});
            skFitSpline(sketch, "E313", {"points": [v(783.8, -516.78) * mm, v(774.9, -512.4) * mm, v(761.34, -500.58) * mm, v(753.67, -490.53) * mm]});
            skFitSpline(sketch, "E314", {"points": [v(753.67, -490.53) * mm, v(740.35, -473.06) * mm, v(739.65, -469.26) * mm, v(737.76, -404.75) * mm]});
            skFitSpline(sketch, "E315", {"points": [v(737.76, -404.75) * mm, v(735.98, -343.84) * mm, v(734.86, -337) * mm, v(726.31, -334.77) * mm]});
            skFitSpline(sketch, "E316", {"points": [v(726.31, -334.77) * mm, v(720.38, -333.22) * mm, v(716.83, -327.8) * mm, v(716.83, -320.28) * mm]});
            skFitSpline(sketch, "E317", {"points": [v(716.83, -320.28) * mm, v(716.83, -308.61) * mm, v(718.01, -308.26) * mm, v(757.5, -308.26) * mm]});
            skFitSpline(sketch, "E318", {"points": [v(757.5, -308.26) * mm, v(796.8, -308.26) * mm, v(798.12, -308.65) * mm, v(796.57, -319.6) * mm]});
            skFitSpline(sketch, "E319", {"points": [v(796.57, -319.6) * mm, v(795.53, -326.9) * mm, v(790.9, -331.52) * mm, v(783.62, -332.56) * mm]});
            skFitSpline(sketch, "E320", {"points": [v(783.62, -332.56) * mm, v(772.64, -334.11) * mm, v(772.28, -335.96) * mm, v(772.28, -389.42) * mm]});
            skFitSpline(sketch, "E321", {"points": [v(772.28, -389.42) * mm, v(772.28, -469.59) * mm, v(783.2, -489.91) * mm, v(826.13, -489.55) * mm]});
            skFitSpline(sketch, "E322", {"points": [v(826.13, -489.55) * mm, v(864.7, -489.23) * mm, v(873.08, -472.6) * mm, v(873.08, -396.33) * mm]});
            skFitSpline(sketch, "E323", {"points": [v(873.08, -396.33) * mm, v(873.08, -341.8) * mm, v(872.35, -337.37) * mm, v(863, -334.93) * mm]});
            skFitSpline(sketch, "E324", {"points": [v(863, -334.93) * mm, v(856.48, -333.22) * mm, v(852.92, -328.05) * mm, v(852.92, -320.28) * mm]});
            skFitSpline(sketch, "E325", {"points": [v(852.92, -320.28) * mm, v(852.92, -308.62) * mm, v(854.12, -308.26) * mm, v(893.24, -308.26) * mm]});
            skFitSpline(sketch, "E326", {"points": [v(893.24, -308.26) * mm, v(930.37, -308.26) * mm, v(933.57, -309.07) * mm, v(933.57, -318.47) * mm]});
            skFitSpline(sketch, "E327", {"points": [v(933.57, -318.47) * mm, v(933.57, -324.72) * mm, v(928.68, -330.53) * mm, v(920.96, -333.47) * mm]});
            skFitSpline(sketch, "E328", {"points": [v(920.96, -333.47) * mm, v(908.44, -338.23) * mm, v(908.36, -338.66) * mm, v(908.36, -401.72) * mm]});
            skFitSpline(sketch, "E329", {"points": [v(908.36, -401.72) * mm, v(908.36, -466.6) * mm, v(905.91, -477.42) * mm, v(886.31, -498.98) * mm]});
            skFitSpline(sketch, "E330", {"points": [v(886.31, -498.98) * mm, v(863.43, -524.14) * mm, v(815.58, -532.45) * mm, v(783.8, -516.78) * mm]});
            skFitSpline(sketch, "E331", {"points": [v(1061.42, -521.81) * mm, v(1055.5, -520.5) * mm, v(1041.55, -511.6) * mm, v(1030.4, -502.06) * mm]});
            skFitSpline(sketch, "E332", {"points": [v(1030.4, -502.06) * mm, v(1000.08, -476.1) * mm, v(987.29, -429.02) * mm, v(997.15, -379.68) * mm]});
            skFitSpline(sketch, "E333", {"points": [v(997.15, -379.68) * mm, v(1001.33, -358.81) * mm, v(1031.15, -324.9) * mm, v(1053.8, -315.27) * mm]});
            skFitSpline(sketch, "E334", {"points": [v(1053.8, -315.27) * mm, v(1076.33, -305.7) * mm, v(1120.3, -304.48) * mm, v(1149.04, -312.65) * mm]});
            skFitSpline(sketch, "E335", {"points": [v(1170.46, -348.78) * mm, v(1170.46, -374.36) * mm, v(1169.1, -378.83) * mm, v(1161.39, -378.83) * mm]});
            skFitSpline(sketch, "E336", {"points": [v(1161.39, -378.83) * mm, v(1149.14, -378.83) * mm, v(1140.22, -369.1) * mm, v(1140.22, -355.73) * mm]});
            skFitSpline(sketch, "E337", {"points": [v(1140.22, -355.73) * mm, v(1140.22, -336.47) * mm, v(1093.3, -331.8) * mm, v(1066.15, -348.36) * mm]});
            skFitSpline(sketch, "E338", {"points": [v(1066.15, -348.36) * mm, v(1043.59, -362.12) * mm, v(1034.12, -378.8) * mm, v(1031.22, -409.94) * mm]});
            skFitSpline(sketch, "E339", {"points": [v(1031.22, -409.94) * mm, v(1028.35, -440.7) * mm, v(1038.26, -464.98) * mm, v(1060.3, -481.12) * mm]});
            skFitSpline(sketch, "E340", {"points": [v(1060.3, -481.12) * mm, v(1078.94, -494.78) * mm, v(1121.23, -494.47) * mm, v(1140.06, -480.55) * mm]});
            skFitSpline(sketch, "E341", {"points": [v(1140.06, -480.55) * mm, v(1152.71, -471.2) * mm, v(1155.06, -470.93) * mm, v(1164.77, -477.73) * mm]});
            skFitSpline(sketch, "E342", {"points": [v(1164.77, -477.73) * mm, v(1179.9, -488.33) * mm, v(1178.36, -492.82) * mm, v(1154.4, -507.95) * mm]});
            skFitSpline(sketch, "E343", {"points": [v(1154.4, -507.95) * mm, v(1133.44, -521.18) * mm, v(1088.57, -527.87) * mm, v(1061.42, -521.81) * mm]});
            skFitSpline(sketch, "E344", {"points": [v(1286.39, -511.92) * mm, v(1286.39, -503.1) * mm, v(1289.66, -498) * mm, v(1296.47, -496.22) * mm]});
            skFitSpline(sketch, "E345", {"points": [v(1296.47, -496.22) * mm, v(1306, -493.72) * mm, v(1306.55, -489.34) * mm, v(1306.55, -416.04) * mm]});
            skFitSpline(sketch, "E346", {"points": [v(1287.58, -338.5) * mm, v(1272.75, -338.5) * mm, v(1267.53, -340.98) * mm, v(1263.64, -349.85) * mm]});
            skFitSpline(sketch, "E347", {"points": [v(1263.64, -349.85) * mm, v(1260.9, -356.08) * mm, v(1253.56, -361.91) * mm, v(1247.32, -362.8) * mm]});
            skFitSpline(sketch, "E348", {"points": [v(1247.32, -362.8) * mm, v(1236.73, -364.3) * mm, v(1235.98, -362.57) * mm, v(1235.98, -336.34) * mm]});
            skFitSpline(sketch, "E349", {"points": [v(1412.4, -335.99) * mm, v(1412.4, -360.45) * mm, v(1411.2, -363.7) * mm, v(1402.2, -363.7) * mm]});
            skFitSpline(sketch, "E350", {"points": [v(1402.2, -363.7) * mm, v(1396.23, -363.7) * mm, v(1389.64, -358.5) * mm, v(1386.28, -351.1) * mm]});
            skFitSpline(sketch, "E351", {"points": [v(1386.28, -351.1) * mm, v(1381.6, -340.85) * mm, v(1376.93, -338.5) * mm, v(1361.18, -338.5) * mm]});
            skFitSpline(sketch, "E352", {"points": [v(1341.83, -416.04) * mm, v(1341.83, -489.34) * mm, v(1342.38, -493.72) * mm, v(1351.91, -496.22) * mm]});
            skFitSpline(sketch, "E353", {"points": [v(1351.91, -496.22) * mm, v(1358.72, -498) * mm, v(1362, -503.1) * mm, v(1362, -511.92) * mm]});
            skFitSpline(sketch, "E354", {"points": [v(1362, -511.92) * mm, v(1362, -524.83) * mm, v(1361.52, -525) * mm, v(1324.19, -525) * mm]});
            skFitSpline(sketch, "E355", {"points": [v(1324.19, -525) * mm, v(1286.86, -525) * mm, v(1286.39, -524.83) * mm, v(1286.39, -511.92) * mm]});
            skFitSpline(sketch, "E356", {"points": [v(1494.3, -519.36) * mm, v(1478.18, -514.7) * mm, v(1477.92, -514.16) * mm, v(1477.92, -484.53) * mm]});
            skFitSpline(sketch, "E357", {"points": [v(1477.92, -484.53) * mm, v(1477.92, -455.88) * mm, v(1478.52, -454.43) * mm, v(1490.38, -454.43) * mm]});
            skFitSpline(sketch, "E358", {"points": [v(1490.38, -454.43) * mm, v(1500.2, -454.43) * mm, v(1503.72, -457.89) * mm, v(1507.05, -470.81) * mm]});
            skFitSpline(sketch, "E359", {"points": [v(1507.05, -470.81) * mm, v(1510.48, -484.16) * mm, v(1514.69, -488.05) * mm, v(1529.76, -491.84) * mm]});
            skFitSpline(sketch, "E360", {"points": [v(1529.76, -491.84) * mm, v(1576.47, -503.56) * mm, v(1602.37, -454.15) * mm, v(1559.13, -435.8) * mm]});
            skFitSpline(sketch, "E361", {"points": [v(1559.13, -435.8) * mm, v(1504.57, -412.67) * mm, v(1498.15, -408.7) * mm, v(1490.18, -393.3) * mm]});
            skFitSpline(sketch, "E362", {"points": [v(1490.18, -393.3) * mm, v(1474.52, -363.01) * mm, v(1487.88, -324.36) * mm, v(1518.24, -312.1) * mm]});
            skFitSpline(sketch, "E363", {"points": [v(1518.24, -312.1) * mm, v(1534.37, -305.6) * mm, v(1582.5, -306.11) * mm, v(1600.6, -313) * mm]});
            skFitSpline(sketch, "E364", {"points": [v(1600.6, -313) * mm, v(1613.7, -317.98) * mm, v(1614.44, -319.9) * mm, v(1613.01, -344.78) * mm]});
            skFitSpline(sketch, "E365", {"points": [v(1613.01, -344.78) * mm, v(1611.6, -369.24) * mm, v(1610.53, -371.27) * mm, v(1598.94, -371.27) * mm]});
            skFitSpline(sketch, "E366", {"points": [v(1598.94, -371.27) * mm, v(1588.93, -371.27) * mm, v(1585.86, -368.2) * mm, v(1583.8, -356.15) * mm]});
            skFitSpline(sketch, "E367", {"points": [v(1583.8, -356.15) * mm, v(1581.59, -343.28) * mm, v(1578.66, -340.78) * mm, v(1564.15, -339.4) * mm]});
            skFitSpline(sketch, "E368", {"points": [v(1564.15, -339.4) * mm, v(1539.68, -337.05) * mm, v(1524.43, -342.06) * mm, v(1520.76, -353.64) * mm]});
            skFitSpline(sketch, "E369", {"points": [v(1520.76, -353.64) * mm, v(1514.64, -372.92) * mm, v(1522.7, -382.05) * mm, v(1558.08, -395.93) * mm]});
            skFitSpline(sketch, "E370", {"points": [v(1558.08, -395.93) * mm, v(1601.54, -412.98) * mm, v(1610.1, -422.33) * mm, v(1612.83, -455.77) * mm]});
            skFitSpline(sketch, "E371", {"points": [v(1612.83, -455.77) * mm, v(1615.3, -485.92) * mm, v(1605.33, -503.4) * mm, v(1577.83, -517.13) * mm]});
            skFitSpline(sketch, "E372", {"points": [v(1577.83, -517.13) * mm, v(1560.59, -525.73) * mm, v(1520.11, -526.81) * mm, v(1494.3, -519.36) * mm]});
            skFitSpline(sketch, "E373", {"points": [v(-417.17, -106.74) * mm, v(-441.3, -100.77) * mm, v(-462.6, -75.97) * mm, v(-462.6, -53.82) * mm]});
            skFitSpline(sketch, "E374", {"points": [v(-462.6, -53.82) * mm, v(-462.6, -29.94) * mm, v(-439.27, -4.3) * mm, v(-406.97, 7.31) * mm]});
            skFitSpline(sketch, "E375", {"points": [v(-406.97, 7.31) * mm, v(-387.63, 14.27) * mm, v(-383.64, 17.38) * mm, v(-389.73, 20.78) * mm]});
            skFitSpline(sketch, "E376", {"points": [v(-389.73, 20.78) * mm, v(-403.7, 28.6) * mm, v(-408.17, 48.85) * mm, v(-399.24, 63.96) * mm]});
            skFitSpline(sketch, "E377", {"points": [v(-399.24, 63.96) * mm, v(-382.38, 92.5) * mm, v(-324.9, 117.7) * mm, v(-285.3, 113.9) * mm]});
            skFitSpline(sketch, "E378", {"points": [v(-285.3, 113.9) * mm, v(-233.64, 108.93) * mm, v(-226.8, 72.23) * mm, v(-273.93, 52.78) * mm]});
            skFitSpline(sketch, "E379", {"points": [v(-273.93, 52.78) * mm, v(-286.48, 47.6) * mm, v(-298.1, 44.71) * mm, v(-299.75, 46.36) * mm]});
            skFitSpline(sketch, "E380", {"points": [v(-299.75, 46.36) * mm, v(-301.4, 48.01) * mm, v(-298.46, 50.89) * mm, v(-293.21, 52.75) * mm]});
            skFitSpline(sketch, "E381", {"points": [v(-293.21, 52.75) * mm, v(-278.26, 58.06) * mm, v(-260.99, 75.66) * mm, v(-260.99, 85.58) * mm]});
            skFitSpline(sketch, "E382", {"points": [v(-260.99, 85.58) * mm, v(-260.99, 115.52) * mm, v(-332.28, 109.02) * mm, v(-365.21, 76.08) * mm]});
            skFitSpline(sketch, "E383", {"points": [v(-365.21, 76.08) * mm, v(-388.81, 52.49) * mm, v(-387.48, 38.4) * mm, v(-360.53, 26.73) * mm]});
            skFitSpline(sketch, "E384", {"points": [v(-360.53, 26.73) * mm, v(-316.08, 7.46) * mm, v(-318.93, -0.6) * mm, v(-370.23, -0.73) * mm]});
            skFitSpline(sketch, "E385", {"points": [v(-370.23, -0.73) * mm, v(-395.93, -0.8) * mm, v(-403.93, -2.98) * mm, v(-416.2, -13.3) * mm]});
            skFitSpline(sketch, "E386", {"points": [v(-416.2, -13.3) * mm, v(-433.28, -27.67) * mm, v(-444.02, -50.22) * mm, v(-441.6, -66.6) * mm]});
            skFitSpline(sketch, "E387", {"points": [v(-441.6, -66.6) * mm, v(-436.54, -100.8) * mm, v(-368.46, -110.95) * mm, v(-316.15, -85.31) * mm]});
            skFitSpline(sketch, "E388", {"points": [v(-316.15, -85.31) * mm, v(-300.75, -77.76) * mm, v(-282.69, -65.77) * mm, v(-276.01, -58.66) * mm]});
            skFitSpline(sketch, "E389", {"points": [v(-276.01, -58.66) * mm, v(-265.7, -47.7) * mm, v(-264.8, -44.25) * mm, v(-270.03, -35.87) * mm]});
            skFitSpline(sketch, "E390", {"points": [v(-270.03, -35.87) * mm, v(-278.91, -21.65) * mm, v(-264.1, -22.38) * mm, v(-254.1, -36.65) * mm]});
            skFitSpline(sketch, "E391", {"points": [v(-254.1, -36.65) * mm, v(-246.78, -47.1) * mm, v(-246.47, -46.95) * mm, v(-236.71, -27.83) * mm]});
            skFitSpline(sketch, "E392", {"points": [v(-236.71, -27.83) * mm, v(-223.37, -1.69) * mm, v(-208.3, 11.46) * mm, v(-196.91, 6.86) * mm]});
            skFitSpline(sketch, "E393", {"points": [v(-196.91, 6.86) * mm, v(-188.88, 3.62) * mm, v(-189.19, 2.73) * mm, v(-199.8, -1.35) * mm]});
            skFitSpline(sketch, "E394", {"points": [v(-199.8, -1.35) * mm, v(-210.53, -5.48) * mm, v(-211.29, -7.78) * mm, v(-207.57, -24.79) * mm]});
            skFitSpline(sketch, "E395", {"points": [v(-207.57, -24.79) * mm, v(-205.3, -35.16) * mm, v(-203.36, -52.28) * mm, v(-203.24, -62.83) * mm]});
            skFitSpline(sketch, "E396", {"points": [v(-192.57, -68.9) * mm, v(-186.83, -61.7) * mm, v(-178.64, -44.9) * mm, v(-174.39, -31.6) * mm]});
            skFitSpline(sketch, "E397", {"points": [v(-174.39, -31.6) * mm, v(-167.35, -9.59) * mm, v(-167.38, -6.92) * mm, v(-174.76, -1.89) * mm]});
            skFitSpline(sketch, "E398", {"points": [v(-174.76, -1.89) * mm, v(-181.79, 2.9) * mm, v(-181.37, 3.68) * mm, v(-171.63, 3.94) * mm]});
            skFitSpline(sketch, "E399", {"points": [v(-171.63, 3.94) * mm, v(-163.87, 4.14) * mm, v(-157.4, 10.08) * mm, v(-150.74, 23.14) * mm]});
            skFitSpline(sketch, "E400", {"points": [v(-150.74, 23.14) * mm, v(-138.14, 47.83) * mm, v(-122.47, 61.76) * mm, v(-111.87, 57.7) * mm]});
            skFitSpline(sketch, "E401", {"points": [v(-111.87, 57.7) * mm, v(-105.24, 55.15) * mm, v(-104.32, 51.1) * mm, v(-107.43, 38.18) * mm]});
            skFitSpline(sketch, "E402", {"points": [v(-107.43, 38.18) * mm, v(-109.6, 29.21) * mm, v(-111.33, 15.64) * mm, v(-111.3, 8.02) * mm]});
            skFitSpline(sketch, "E403", {"points": [v(-111.3, 8.02) * mm, v(-111.25, -1.38) * mm, v(-113.84, -5.85) * mm, v(-119.32, -5.85) * mm]});
            skFitSpline(sketch, "E404", {"points": [v(-119.32, -5.85) * mm, v(-134.76, -5.85) * mm, v(-165.22, -52.9) * mm, v(-165.22, -76.74) * mm]});
            skFitSpline(sketch, "E405", {"points": [v(-165.22, -76.74) * mm, v(-165.22, -93.74) * mm, v(-151.84, -87.32) * mm, v(-135.64, -62.55) * mm]});
            skFitSpline(sketch, "E406", {"points": [v(-135.64, -62.55) * mm, v(-127.03, -49.38) * mm, v(-119.96, -42) * mm, v(-119.94, -46.17) * mm]});
            skFitSpline(sketch, "E407", {"points": [v(-119.94, -46.17) * mm, v(-119.88, -57.63) * mm, v(-138.13, -85.12) * mm, v(-150.02, -91.49) * mm]});
            skFitSpline(sketch, "E408", {"points": [v(-150.02, -91.49) * mm, v(-162.87, -98.36) * mm, v(-180.35, -93.63) * mm, v(-180.35, -83.29) * mm]});
            skFitSpline(sketch, "E409", {"points": [v(-180.35, -83.29) * mm, v(-180.35, -77.27) * mm, v(-183.41, -77.9) * mm, v(-195.4, -86.44) * mm]});
            skFitSpline(sketch, "E410", {"points": [v(-195.4, -86.44) * mm, v(-215.75, -100.93) * mm, v(-250.73, -99.03) * mm, v(-258.67, -83) * mm]});
            skFitSpline(sketch, "E411", {"points": [v(-278.95, -81.83) * mm, v(-309.1, -101.96) * mm, v(-382.77, -115.24) * mm, v(-417.17, -106.74) * mm]});
            skFitSpline(sketch, "E412", {"points": [v(-232.38, -41.15) * mm, v(-239.92, -55.74) * mm, v(-240.52, -61.45) * mm, v(-235.78, -73.91) * mm]});
            skFitSpline(sketch, "E413", {"points": [v(-235.78, -73.91) * mm, v(-230.72, -87.21) * mm, v(-229.45, -87.95) * mm, v(-225.08, -80.15) * mm]});
            skFitSpline(sketch, "E414", {"points": [v(-225.08, -80.15) * mm, v(-222.35, -75.27) * mm, v(-220.82, -60.53) * mm, v(-221.68, -47.39) * mm]});
            skFitSpline(sketch, "E415", {"points": [v(-122.47, 25.92) * mm, v(-118.19, 36.17) * mm, v(-115.8, 44.56) * mm, v(-117.14, 44.56) * mm]});
            skFitSpline(sketch, "E416", {"points": [v(-117.14, 44.56) * mm, v(-120.72, 44.56) * mm, v(-134.98, 15.89) * mm, v(-134.98, 8.69) * mm]});
            skFitSpline(sketch, "E417", {"points": [v(-134.98, 8.69) * mm, v(-134.98, -0.26) * mm, v(-131.28, 4.84) * mm, v(-122.47, 25.92) * mm]});
            skFitSpline(sketch, "E418", {"points": [v(-111.14, -95.31) * mm, v(-114.75, -84.96) * mm, v(-109.33, -76.4) * mm, v(-99.16, -76.4) * mm]});
            skFitSpline(sketch, "E419", {"points": [v(-99.16, -76.4) * mm, v(-87.38, -76.4) * mm, v(-86.12, -94.15) * mm, v(-97.6, -98.55) * mm]});
            skFitSpline(sketch, "E420", {"points": [v(-97.6, -98.55) * mm, v(-108.26, -102.65) * mm, v(-108.6, -102.57) * mm, v(-111.14, -95.31) * mm]});
            skFitSpline(sketch, "E421", {"points": [v(24.55, -93.44) * mm, v(11.2, -88.78) * mm, v(2.26, -88.22) * mm, v(-4.1, -91.62) * mm]});
            skFitSpline(sketch, "E422", {"points": [v(-4.1, -91.62) * mm, v(-23.95, -102.24) * mm, v(-18, -94.74) * mm, v(33.09, -44.76) * mm]});
            skFitSpline(sketch, "E423", {"points": [v(33.09, -44.76) * mm, v(82.8, 3.88) * mm, v(97.66, 26) * mm, v(89.5, 39.23) * mm]});
            skFitSpline(sketch, "E424", {"points": [v(89.5, 39.23) * mm, v(81.98, 51.38) * mm, v(66.04, 41.75) * mm, v(44.1, 11.8) * mm]});
            skFitSpline(sketch, "E425", {"points": [v(44.1, 11.8) * mm, v(37.58, 2.9) * mm, v(36.7, 2.75) * mm, v(36.55, 10.46) * mm]});
            skFitSpline(sketch, "E426", {"points": [v(36.55, 10.46) * mm, v(36.25, 26.94) * mm, v(62.52, 50) * mm, v(85.04, 53.03) * mm]});
            skFitSpline(sketch, "E427", {"points": [v(85.04, 53.03) * mm, v(102.63, 55.39) * mm, v(106.84, 54.19) * mm, v(111.5, 45.48) * mm]});
            skFitSpline(sketch, "E428", {"points": [v(111.5, 45.48) * mm, v(121.69, 26.45) * mm, v(105.93, 3.56) * mm, v(47.09, -48.1) * mm]});
            skFitSpline(sketch, "E429", {"points": [v(47.09, -48.1) * mm, v(23.93, -68.42) * mm, v(24.4, -72.64) * mm, v(50.53, -79.6) * mm]});
            skFitSpline(sketch, "E430", {"points": [v(50.53, -79.6) * mm, v(58.69, -81.76) * mm, v(65.82, -79.23) * mm, v(74.47, -71.1) * mm]});
            skFitSpline(sketch, "E431", {"points": [v(74.47, -71.1) * mm, v(81.25, -64.74) * mm, v(86.8, -61.77) * mm, v(86.8, -64.5) * mm]});
            skFitSpline(sketch, "E432", {"points": [v(86.8, -64.5) * mm, v(86.8, -70.67) * mm, v(61.77, -94.18) * mm, v(51.51, -97.65) * mm]});
            skFitSpline(sketch, "E433", {"points": [v(51.51, -97.65) * mm, v(47.35, -99.06) * mm, v(35.22, -97.17) * mm, v(24.55, -93.44) * mm]});
            skFitSpline(sketch, "E434", {"points": [v(135.69, -91.31) * mm, v(110.97, -71.28) * mm, v(128.56, -10.87) * mm, v(171.24, 30.77) * mm]});
            skFitSpline(sketch, "E435", {"points": [v(171.24, 30.77) * mm, v(229.15, 87.26) * mm, v(264, 41.81) * mm, v(222.5, -36.06) * mm]});
            skFitSpline(sketch, "E436", {"points": [v(222.5, -36.06) * mm, v(195.55, -86.6) * mm, v(158.76, -110.02) * mm, v(135.69, -91.31) * mm]});
            skFitSpline(sketch, "E437", {"points": [v(179.86, -74.43) * mm, v(210.64, -41.79) * mm, v(238.35, 35) * mm, v(222.81, 44.6) * mm]});
            skFitSpline(sketch, "E438", {"points": [v(222.81, 44.6) * mm, v(205.98, 55) * mm, v(173.04, 17.67) * mm, v(152.59, -35.01) * mm]});
            skFitSpline(sketch, "E439", {"points": [v(152.59, -35.01) * mm, v(137.35, -74.24) * mm, v(139.15, -89.33) * mm, v(159.28, -91.13) * mm]});
            skFitSpline(sketch, "E440", {"points": [v(159.28, -91.13) * mm, v(161.73, -91.35) * mm, v(170.99, -83.83) * mm, v(179.86, -74.43) * mm]});
            skFitSpline(sketch, "E441", {"points": [v(336.7, -97.22) * mm, v(335.2, -94.8) * mm, v(342.76, -91.65) * mm, v(353.5, -90.21) * mm]});
            skFitSpline(sketch, "E442", {"points": [v(353.5, -90.21) * mm, v(364.22, -88.77) * mm, v(379.83, -82.55) * mm, v(388.16, -76.39) * mm]});
            skFitSpline(sketch, "E443", {"points": [v(388.16, -76.39) * mm, v(405.08, -63.88) * mm, v(422.58, -30.1) * mm, v(416.9, -20.92) * mm]});
            skFitSpline(sketch, "E444", {"points": [v(416.9, -20.92) * mm, v(413.1, -14.76) * mm, v(389.26, -16.16) * mm, v(372.02, -23.57) * mm]});
            skFitSpline(sketch, "E445", {"points": [v(372.02, -23.57) * mm, v(364, -27.02) * mm, v(365.16, -22.68) * mm, v(378.99, 2.48) * mm]});
            skFitSpline(sketch, "E446", {"points": [v(378.99, 2.48) * mm, v(406.08, 51.76) * mm, v(405.97, 51.67) * mm, v(439.7, 52.73) * mm]});
            skFitSpline(sketch, "E447", {"points": [v(439.7, 52.73) * mm, v(456.3, 53.25) * mm, v(469.86, 52.01) * mm, v(469.86, 49.97) * mm]});
            skFitSpline(sketch, "E448", {"points": [v(469.86, 49.97) * mm, v(469.86, 43.39) * mm, v(447.72, 34.79) * mm, v(427.08, 33.35) * mm]});
            skFitSpline(sketch, "E449", {"points": [v(427.08, 33.35) * mm, v(409.42, 32.13) * mm, v(405.63, 29.5) * mm, v(395.88, 11.8) * mm]});
            skFitSpline(sketch, "E450", {"points": [v(407.82, -8.37) * mm, v(447.46, -8.37) * mm, v(450.53, -36.06) * mm, v(414.63, -69.87) * mm]});
            skFitSpline(sketch, "E451", {"points": [v(414.63, -69.87) * mm, v(390.68, -92.42) * mm, v(343.88, -108.85) * mm, v(336.7, -97.22) * mm]});
            skFitSpline(sketch, "E452", {"points": [v(261.24, -80.19) * mm, v(265.85, -71.18) * mm, v(279.52, -46.57) * mm, v(291.61, -25.51) * mm]});
            skFitSpline(sketch, "E453", {"points": [v(291.61, -25.51) * mm, v(303.71, -4.45) * mm, v(313.6, 14.33) * mm, v(313.6, 16.22) * mm]});
            skFitSpline(sketch, "E454", {"points": [v(313.6, 16.22) * mm, v(313.6, 18.11) * mm, v(306.83, 14.65) * mm, v(298.55, 8.52) * mm]});
            skFitSpline(sketch, "E455", {"points": [v(298.55, 8.52) * mm, v(271.04, -11.81) * mm, v(278.3, 1.7) * mm, v(309.22, 28.37) * mm]});
            skFitSpline(sketch, "E456", {"points": [v(309.22, 28.37) * mm, v(355.96, 68.69) * mm, v(359.25, 63.16) * mm, v(325.86, 0.46) * mm]});
            skFitSpline(sketch, "E457", {"points": [v(325.86, 0.46) * mm, v(278.88, -87.75) * mm, v(273.13, -96.57) * mm, v(262.6, -96.57) * mm]});
            skFitSpline(sketch, "E458", {"points": [v(262.6, -96.57) * mm, v(253.26, -96.57) * mm, v(253.2, -95.9) * mm, v(261.24, -80.19) * mm]});
            skFitSpline(sketch, "E459", {"points": [v(-1668.5, 180.47) * mm, v(-1739.88, 313.56) * mm, v(-1798.28, 424.38) * mm, v(-1798.28, 426.75) * mm]});
            skFitSpline(sketch, "E460", {"points": [v(-1798.28, 426.75) * mm, v(-1798.28, 430.91) * mm, v(-1772.95, 444.58) * mm, v(-1770.62, 441.67) * mm]});
            skFitSpline(sketch, "E461", {"points": [v(-1770.62, 441.67) * mm, v(-1769.99, 440.87) * mm, v(-1714.46, 337.59) * mm, v(-1647.23, 212.15) * mm]});
            skFitSpline(sketch, "E462", {"points": [v(-1647.23, 212.15) * mm, v(-1580, 86.7) * mm, v(-1523.46, -15.93) * mm, v(-1521.58, -15.93) * mm]});
            skFitSpline(sketch, "E463", {"points": [v(-1521.58, -15.93) * mm, v(-1519.71, -15.93) * mm, v(-1486.51, 1.03) * mm, v(-1447.8, 21.75) * mm]});
            skFitSpline(sketch, "E464", {"points": [v(-1368.7, 48.21) * mm, v(-1363.92, 42.04) * mm, v(-1359.95, 35.82) * mm, v(-1359.89, 34.39) * mm]});
            skFitSpline(sketch, "E465", {"points": [v(-1359.89, 34.39) * mm, v(-1359.78, 31.75) * mm, v(-1523.9, -57.6) * mm, v(-1533.53, -60.14) * mm]});
            skFitSpline(sketch, "E466", {"points": [v(-1533.53, -60.14) * mm, v(-1536.38, -60.9) * mm, v(-1597.11, 47.38) * mm, v(-1668.5, 180.47) * mm]});
            skFitSpline(sketch, "E467", {"points": [v(1490.32, 30.62) * mm, v(1499.42, 64.62) * mm, v(1509.38, 101.45) * mm, v(1512.45, 112.45) * mm]});
            skFitSpline(sketch, "E468", {"points": [v(1512.45, 112.45) * mm, v(1515.53, 123.46) * mm, v(1516.39, 133.99) * mm, v(1514.36, 135.86) * mm]});
            skFitSpline(sketch, "E469", {"points": [v(1514.36, 135.86) * mm, v(1512.34, 137.73) * mm, v(1484.85, 152.9) * mm, v(1453.27, 169.57) * mm]});
            skFitSpline(sketch, "E470", {"points": [v(1343.8, 137.73) * mm, v(1315.16, 103.55) * mm, v(1289.44, 74.17) * mm, v(1286.64, 72.44) * mm]});
            skFitSpline(sketch, "E471", {"points": [v(1286.64, 72.44) * mm, v(1282.47, 69.86) * mm, v(1264.62, 76.08) * mm, v(1256.77, 82.84) * mm]});
            skFitSpline(sketch, "E472", {"points": [v(1256.77, 82.84) * mm, v(1254.6, 84.71) * mm, v(1364.79, 216.53) * mm, v(1520.2, 397.99) * mm]});
            skFitSpline(sketch, "E473", {"points": [v(1520.2, 397.99) * mm, v(1618.96, 513.3) * mm, v(1627.29, 521.71) * mm, v(1637.89, 516.88) * mm]});
            skFitSpline(sketch, "E474", {"points": [v(1637.89, 516.88) * mm, v(1644.16, 514.03) * mm, v(1649.29, 509.77) * mm, v(1649.29, 507.43) * mm]});
            skFitSpline(sketch, "E475", {"points": [v(1649.29, 507.43) * mm, v(1649.29, 505.08) * mm, v(1617.54, 380.87) * mm, v(1578.73, 231.4) * mm]});
            skFitSpline(sketch, "E476", {"points": [v(1578.73, 231.4) * mm, v(1539.92, 81.94) * mm, v(1508.16, -41.66) * mm, v(1508.16, -43.26) * mm]});
            skFitSpline(sketch, "E477", {"points": [v(1508.16, -43.26) * mm, v(1508.16, -47.83) * mm, v(1501.7, -46.36) * mm, v(1487.2, -38.48) * mm]});
            skFitSpline(sketch, "E478", {"points": [v(1560.78, 301.6) * mm, v(1586.8, 403.26) * mm, v(1591.59, 427.53) * mm, v(1584.12, 419.76) * mm]});
            skFitSpline(sketch, "E479", {"points": [v(1584.12, 419.76) * mm, v(1563.25, 398.05) * mm, v(1422.48, 229.94) * mm, v(1422.48, 226.72) * mm]});
            skFitSpline(sketch, "E480", {"points": [v(1422.48, 226.72) * mm, v(1422.48, 223.44) * mm, v(1524.56, 170.62) * mm, v(1526.92, 172.67) * mm]});
            skFitSpline(sketch, "E481", {"points": [v(1526.92, 172.67) * mm, v(1527.54, 173.2) * mm, v(1542.78, 231.22) * mm, v(1560.78, 301.6) * mm]});
            skFitSpline(sketch, "E482", {"points": [v(-1029.88, -30.65) * mm, v(-1031.76, -27.61) * mm, v(-1031.2, -23.04) * mm, v(-1028.65, -20.48) * mm]});
            skFitSpline(sketch, "E483", {"points": [v(-1028.65, -20.48) * mm, v(-1025.9, -17.73) * mm, v(-920.15, -16.37) * mm, v(-769.76, -17.14) * mm]});
            skFitSpline(sketch, "E484", {"points": [v(-769.76, -17.14) * mm, v(-547.71, -18.28) * mm, v(-515.53, -19.4) * mm, v(-515.53, -26) * mm]});
            skFitSpline(sketch, "E485", {"points": [v(-515.53, -26) * mm, v(-515.53, -32.61) * mm, v(-547.85, -33.73) * mm, v(-771, -34.87) * mm]});
            skFitSpline(sketch, "E486", {"points": [v(-771, -34.87) * mm, v(-952.12, -35.8) * mm, v(-1027.46, -34.57) * mm, v(-1029.88, -30.65) * mm]});
            skFitSpline(sketch, "E487", {"points": [v(497.33, -30.65) * mm, v(495.46, -27.61) * mm, v(496.01, -23.04) * mm, v(498.57, -20.48) * mm]});
            skFitSpline(sketch, "E488", {"points": [v(498.57, -20.48) * mm, v(501.32, -17.73) * mm, v(611.06, -16.37) * mm, v(767.53, -17.14) * mm]});
            skFitSpline(sketch, "E489", {"points": [v(767.53, -17.14) * mm, v(998.54, -18.28) * mm, v(1031.85, -19.4) * mm, v(1031.85, -26) * mm]});
            skFitSpline(sketch, "E490", {"points": [v(1031.85, -26) * mm, v(1031.85, -32.61) * mm, v(998.4, -33.73) * mm, v(766.3, -34.87) * mm]});
            skFitSpline(sketch, "E491", {"points": [v(766.3, -34.87) * mm, v(577.9, -35.8) * mm, v(499.76, -34.57) * mm, v(497.33, -30.65) * mm]});
            skFitSpline(sketch, "E492", {"points": [v(-1308.05, 71.02) * mm, v(-1317.22, 90.48) * mm, v(-1531.82, 555.85) * mm, v(-1534.26, 561.55) * mm]});
            skFitSpline(sketch, "E493", {"points": [v(-1534.26, 561.55) * mm, v(-1537.12, 568.22) * mm, v(-1510.88, 580.86) * mm, v(-1505.73, 575.3) * mm]});
            skFitSpline(sketch, "E494", {"points": [v(-1505.73, 575.3) * mm, v(-1500.71, 569.88) * mm, v(-1273.32, 73.82) * mm, v(-1275.16, 72.31) * mm]});
            skFitSpline(sketch, "E495", {"points": [v(-1275.16, 72.31) * mm, v(-1278.16, 69.86) * mm, v(-1298.71, 59.68) * mm, v(-1300.67, 59.68) * mm]});
            skFitSpline(sketch, "E496", {"points": [v(-1300.67, 59.68) * mm, v(-1301.8, 59.68) * mm, v(-1305.12, 64.78) * mm, v(-1308.05, 71.02) * mm]});
            skFitSpline(sketch, "E497", {"points": [v(-1212.73, 126.32) * mm, v(-1289.3, 320.52) * mm, v(-1402.12, 627.36) * mm, v(-1397.88, 629.88) * mm]});
            skFitSpline(sketch, "E498", {"points": [v(-1397.88, 629.88) * mm, v(-1394.94, 631.63) * mm, v(-1387.77, 634.5) * mm, v(-1381.95, 636.29) * mm]});
            skFitSpline(sketch, "E499", {"points": [v(-1381.95, 636.29) * mm, v(-1372.14, 639.28) * mm, v(-1367.5, 629.29) * mm, v(-1318.94, 500.8) * mm]});
            skFitSpline(sketch, "E500", {"points": [v(-1318.94, 500.8) * mm, v(-1278.6, 394.03) * mm, v(-1265.7, 364.7) * mm, v(-1262.93, 373.44) * mm]});
            skFitSpline(sketch, "E501", {"points": [v(-1262.93, 373.44) * mm, v(-1260.95, 379.68) * mm, v(-1245.5, 457.32) * mm, v(-1228.57, 545.99) * mm]});
            skFitSpline(sketch, "E502", {"points": [v(-1228.57, 545.99) * mm, v(-1211.65, 634.65) * mm, v(-1197.4, 707.46) * mm, v(-1196.89, 707.79) * mm]});
            skFitSpline(sketch, "E503", {"points": [v(-1196.89, 707.79) * mm, v(-1193.1, 710.23) * mm, v(-1161.3, 719.74) * mm, v(-1160.32, 718.72) * mm]});
            skFitSpline(sketch, "E504", {"points": [v(-1160.32, 718.72) * mm, v(-1159.63, 718.02) * mm, v(-1172.6, 648.47) * mm, v(-1189.13, 564.17) * mm]});
            skFitSpline(sketch, "E505", {"points": [v(-1189.13, 564.17) * mm, v(-1205.93, 478.52) * mm, v(-1217.17, 409.6) * mm, v(-1214.63, 407.92) * mm]});
            skFitSpline(sketch, "E506", {"points": [v(-1214.63, 407.92) * mm, v(-1212.12, 406.28) * mm, v(-1154.14, 358.59) * mm, v(-1085.78, 301.94) * mm]});
            skFitSpline(sketch, "E507", {"points": [v(-977.92, 191.96) * mm, v(-989.94, 186.86) * mm, v(-996.7, 186.43) * mm, v(-1003.1, 190.37) * mm]});
            skFitSpline(sketch, "E508", {"points": [v(-1003.1, 190.37) * mm, v(-1007.9, 193.33) * mm, v(-1058.46, 234.31) * mm, v(-1115.46, 281.44) * mm]});
            skFitSpline(sketch, "E509", {"points": [v(-1115.46, 281.44) * mm, v(-1172.45, 328.58) * mm, v(-1220.87, 367.14) * mm, v(-1223.05, 367.14) * mm]});
            skFitSpline(sketch, "E510", {"points": [v(-1223.05, 367.14) * mm, v(-1225.23, 367.14) * mm, v(-1230.38, 351.45) * mm, v(-1234.5, 332.29) * mm]});
            skFitSpline(sketch, "E511", {"points": [v(-1207.8, 207.8) * mm, v(-1188.99, 158.5) * mm, v(-1174.1, 117.94) * mm, v(-1174.7, 117.66) * mm]});
            skFitSpline(sketch, "E512", {"points": [v(-1174.7, 117.66) * mm, v(-1205.1, 103.87) * mm, v(-1203.75, 103.56) * mm, v(-1212.73, 126.32) * mm]});
            skFitSpline(sketch, "E513", {"points": [v(1081.73, 199.6) * mm, v(1090.92, 221.05) * mm, v(1139.77, 335.56) * mm, v(1190.3, 454.04) * mm]});
            skFitSpline(sketch, "E514", {"points": [v(1190.3, 454.04) * mm, v(1240.84, 572.53) * mm, v(1284.04, 670.63) * mm, v(1286.3, 672.02) * mm]});
            skFitSpline(sketch, "E515", {"points": [v(1286.3, 672.02) * mm, v(1294.82, 677.29) * mm, v(1404.4, 624.2) * mm, v(1424.08, 605.28) * mm]});
            skFitSpline(sketch, "E516", {"points": [v(1424.08, 605.28) * mm, v(1462.02, 568.8) * mm, v(1471.42, 524.84) * mm, v(1452.84, 470.82) * mm]});
            skFitSpline(sketch, "E517", {"points": [v(1452.84, 470.82) * mm, v(1430.7, 406.44) * mm, v(1396.04, 365.36) * mm, v(1353.37, 352.9) * mm]});
            skFitSpline(sketch, "E518", {"points": [v(1353.37, 352.9) * mm, v(1325.18, 344.66) * mm, v(1284.37, 351.44) * mm, v(1238.92, 371.92) * mm]});
            skFitSpline(sketch, "E519", {"points": [v(1238.92, 371.92) * mm, v(1219.75, 380.56) * mm, v(1202.42, 385.86) * mm, v(1200.4, 383.69) * mm]});
            skFitSpline(sketch, "E520", {"points": [v(1200.4, 383.69) * mm, v(1198.4, 381.51) * mm, v(1174.7, 328.1) * mm, v(1147.73, 265) * mm]});
            skFitSpline(sketch, "E521", {"points": [v(1147.73, 265) * mm, v(1120.76, 201.9) * mm, v(1097.26, 149.37) * mm, v(1095.5, 148.28) * mm]});
            skFitSpline(sketch, "E522", {"points": [v(1095.5, 148.28) * mm, v(1093.74, 147.2) * mm, v(1086.16, 149.52) * mm, v(1078.67, 153.44) * mm]});
            skFitSpline(sketch, "E523", {"points": [v(1355.94, 389.34) * mm, v(1376.86, 400.22) * mm, v(1390.13, 416.9) * mm, v(1407.64, 454.35) * mm]});
            skFitSpline(sketch, "E524", {"points": [v(1407.64, 454.35) * mm, v(1418.4, 477.35) * mm, v(1424.54, 499.41) * mm, v(1426.3, 521.33) * mm]});
            skFitSpline(sketch, "E525", {"points": [v(1406.64, 575.24) * mm, v(1392.54, 588.67) * mm, v(1369.75, 602.5) * mm, v(1344.63, 612.87) * mm]});
            skFitSpline(sketch, "E526", {"points": [v(1344.63, 612.87) * mm, v(1322.78, 621.9) * mm, v(1304.31, 628.68) * mm, v(1303.58, 627.95) * mm]});
            skFitSpline(sketch, "E527", {"points": [v(1303.58, 627.95) * mm, v(1301.23, 625.6) * mm, v(1215.82, 425.57) * mm, v(1215.82, 422.42) * mm]});
            skFitSpline(sketch, "E528", {"points": [v(1215.82, 422.42) * mm, v(1215.82, 419.88) * mm, v(1275.63, 394.16) * mm, v(1301.5, 385.56) * mm]});
            skFitSpline(sketch, "E529", {"points": [v(1301.5, 385.56) * mm, v(1316.5, 380.59) * mm, v(1342.6, 382.4) * mm, v(1355.94, 389.34) * mm]});
            skFitSpline(sketch, "E530", {"points": [v(-932.97, 234.83) * mm, v(-961.32, 331.02) * mm, v(-1073.6, 745.72) * mm, v(-1071.79, 747.53) * mm]});
            skFitSpline(sketch, "E531", {"points": [v(-1071.79, 747.53) * mm, v(-1069.11, 750.2) * mm, v(-888.52, 800.6) * mm, v(-881.62, 800.6) * mm]});
            skFitSpline(sketch, "E532", {"points": [v(-881.62, 800.6) * mm, v(-879.02, 800.6) * mm, v(-874.6, 794.01) * mm, v(-871.79, 785.96) * mm]});
            skFitSpline(sketch, "E533", {"points": [v(-871.79, 785.96) * mm, v(-867.56, 773.83) * mm, v(-868.12, 770.92) * mm, v(-875.07, 769.03) * mm]});
            skFitSpline(sketch, "E534", {"points": [v(-875.07, 769.03) * mm, v(-879.7, 767.78) * mm, v(-915.22, 758.19) * mm, v(-954.03, 747.72) * mm]});
            skFitSpline(sketch, "E535", {"points": [v(-954.03, 747.72) * mm, v(-992.84, 737.25) * mm, v(-1026.48, 727) * mm, v(-1028.78, 724.93) * mm]});
            skFitSpline(sketch, "E536", {"points": [v(-1028.78, 724.93) * mm, v(-1032.73, 721.38) * mm, v(-978.89, 514.31) * mm, v(-972.27, 507.64) * mm]});
            skFitSpline(sketch, "E537", {"points": [v(-972.27, 507.64) * mm, v(-970.56, 505.9) * mm, v(-938.53, 513.22) * mm, v(-901.1, 523.88) * mm]});
            skFitSpline(sketch, "E538", {"points": [v(-901.1, 523.88) * mm, v(-863.68, 534.55) * mm, v(-832.72, 543.34) * mm, v(-832.3, 543.41) * mm]});
            skFitSpline(sketch, "E539", {"points": [v(-832.3, 543.41) * mm, v(-831.87, 543.49) * mm, v(-829.12, 536.64) * mm, v(-826.18, 528.2) * mm]});
            skFitSpline(sketch, "E540", {"points": [v(-826.18, 528.2) * mm, v(-822.16, 516.68) * mm, v(-822.35, 512.28) * mm, v(-826.95, 510.58) * mm]});
            skFitSpline(sketch, "E541", {"points": [v(-826.95, 510.58) * mm, v(-830.31, 509.33) * mm, v(-861.08, 500.5) * mm, v(-895.33, 490.96) * mm]});
            skFitSpline(sketch, "E542", {"points": [v(-895.33, 490.96) * mm, v(-929.58, 481.42) * mm, v(-958.8, 472.4) * mm, v(-960.29, 470.93) * mm]});
            skFitSpline(sketch, "E543", {"points": [v(-960.29, 470.93) * mm, v(-962.48, 468.73) * mm, v(-907.4, 257.8) * mm, v(-903.12, 252) * mm]});
            skFitSpline(sketch, "E544", {"points": [v(-903.12, 252) * mm, v(-902.42, 251.04) * mm, v(-864.84, 260.52) * mm, v(-819.62, 273.05) * mm]});
            skFitSpline(sketch, "E545", {"points": [v(-819.62, 273.05) * mm, v(-774.4, 285.58) * mm, v(-736.84, 295.27) * mm, v(-736.14, 294.58) * mm]});
            skFitSpline(sketch, "E546", {"points": [v(-736.14, 294.58) * mm, v(-735.45, 293.89) * mm, v(-733.54, 286.6) * mm, v(-731.9, 278.38) * mm]});
            skFitSpline(sketch, "E547", {"points": [v(-824.46, 237.16) * mm, v(-877.02, 222.71) * mm, v(-921.34, 210.89) * mm, v(-922.97, 210.89) * mm]});
            skFitSpline(sketch, "E548", {"points": [v(-922.97, 210.89) * mm, v(-924.6, 210.89) * mm, v(-929.1, 221.66) * mm, v(-932.98, 234.83) * mm]});
            skFitSpline(sketch, "E549", {"points": [v(831, 234.22) * mm, v(786.53, 248.55) * mm, v(776.75, 253.44) * mm, v(778.68, 260.35) * mm]});
            skFitSpline(sketch, "E550", {"points": [v(778.68, 260.35) * mm, v(791.1, 304.97) * mm, v(941.2, 778.94) * mm, v(943.91, 782.1) * mm]});
            skFitSpline(sketch, "E551", {"points": [v(943.91, 782.1) * mm, v(948.67, 787.68) * mm, v(1042.46, 758.47) * mm, v(1070.99, 742.52) * mm]});
            skFitSpline(sketch, "E552", {"points": [v(1070.99, 742.52) * mm, v(1122.9, 713.5) * mm, v(1140.7, 659.51) * mm, v(1122.24, 587.12) * mm]});
            skFitSpline(sketch, "E553", {"points": [v(1122.24, 587.12) * mm, v(1099, 496.05) * mm, v(1032.48, 298.17) * mm, v(1016.93, 273.86) * mm]});
            skFitSpline(sketch, "E554", {"points": [v(1016.93, 273.86) * mm, v(977.68, 212.5) * mm, v(929.94, 202.33) * mm, v(831, 234.22) * mm]});
            skFitSpline(sketch, "E555", {"points": [v(965.62, 266.4) * mm, v(975.13, 274.74) * mm, v(987.5, 291.32) * mm, v(993.1, 303.24) * mm]});
            skFitSpline(sketch, "E556", {"points": [v(993.1, 303.24) * mm, v(1013.43, 346.5) * mm, v(1091.08, 601.06) * mm, v(1093.3, 631.75) * mm]});
            skFitSpline(sketch, "E557", {"points": [v(1093.3, 631.75) * mm, v(1097.12, 684.48) * mm, v(1074.86, 710.48) * mm, v(1009.12, 730.06) * mm]});
            skFitSpline(sketch, "E558", {"points": [v(1009.12, 730.06) * mm, v(990.53, 735.6) * mm, v(973.22, 740.12) * mm, v(970.65, 740.12) * mm]});
            skFitSpline(sketch, "E559", {"points": [v(970.65, 740.12) * mm, v(965.79, 740.12) * mm, v(819.24, 277.98) * mm, v(823.04, 274.63) * mm]});
            skFitSpline(sketch, "E560", {"points": [v(823.04, 274.63) * mm, v(831.1, 267.52) * mm, v(895.78, 252.18) * mm, v(919.53, 251.74) * mm]});
            skFitSpline(sketch, "E561", {"points": [v(919.53, 251.74) * mm, v(944.77, 251.28) * mm, v(950.48, 253.1) * mm, v(965.62, 266.4) * mm]});
            skFitSpline(sketch, "E562", {"points": [v(692.9, 270.2) * mm, v(686.65, 271.23) * mm, v(681.55, 273.37) * mm, v(681.55, 274.95) * mm]});
            skFitSpline(sketch, "E563", {"points": [v(681.55, 274.95) * mm, v(681.55, 279.02) * mm, v(606.94, 686.4) * mm, v(600.05, 719.96) * mm]});
            skFitSpline(sketch, "E564", {"points": [v(600.05, 719.96) * mm, v(592.82, 755.12) * mm, v(596.62, 769.2) * mm, v(544.92, 515.3) * mm]});
            skFitSpline(sketch, "E565", {"points": [v(544.92, 515.3) * mm, v(506.26, 325.43) * mm, v(502.76, 311.7) * mm, v(492.96, 311.77) * mm]});
            skFitSpline(sketch, "E566", {"points": [v(492.96, 311.77) * mm, v(465.97, 311.97) * mm, v(465.13, 304.35) * mm, v(523.97, 591.09) * mm]});
            skFitSpline(sketch, "E567", {"points": [v(523.97, 591.09) * mm, v(554.48, 739.8) * mm, v(580.6, 862.63) * mm, v(582.02, 864.05) * mm]});
            skFitSpline(sketch, "E568", {"points": [v(582.02, 864.05) * mm, v(583.44, 865.46) * mm, v(590.17, 865.22) * mm, v(596.99, 863.5) * mm]});
            skFitSpline(sketch, "E569", {"points": [v(596.99, 863.5) * mm, v(609.12, 860.46) * mm, v(610.27, 855.49) * mm, v(651.77, 626.38) * mm]});
            skFitSpline(sketch, "E570", {"points": [v(651.77, 626.38) * mm, v(675.08, 497.66) * mm, v(695.4, 392.35) * mm, v(696.92, 392.35) * mm]});
            skFitSpline(sketch, "E571", {"points": [v(696.92, 392.35) * mm, v(698.45, 392.34) * mm, v(718.45, 484.77) * mm, v(741.39, 597.73) * mm]});
            skFitSpline(sketch, "E572", {"points": [v(741.39, 597.73) * mm, v(764.32, 710.7) * mm, v(784.2, 807.1) * mm, v(785.58, 811.95) * mm]});
            skFitSpline(sketch, "E573", {"points": [v(785.58, 811.95) * mm, v(788.17, 821.1) * mm, v(814.6, 824.72) * mm, v(819.62, 816.6) * mm]});
            skFitSpline(sketch, "E574", {"points": [v(819.62, 816.6) * mm, v(822.87, 811.34) * mm, v(713.22, 275.55) * mm, v(708.04, 271.4) * mm]});
            skFitSpline(sketch, "E575", {"points": [v(708.04, 271.4) * mm, v(705.95, 269.71) * mm, v(699.13, 269.18) * mm, v(692.9, 270.2) * mm]});
            skFitSpline(sketch, "E576", {"points": [v(-394.56, 330.28) * mm, v(-432.7, 338.03) * mm, v(-464.75, 368.84) * mm, v(-480.46, 412.88) * mm]});
            skFitSpline(sketch, "E577", {"points": [v(-480.46, 412.88) * mm, v(-484.84, 425.15) * mm, v(-496.6, 507.6) * mm, v(-506.62, 596.11) * mm]});
            skFitSpline(sketch, "E578", {"points": [v(-506.62, 596.11) * mm, v(-522.36, 735.26) * mm, v(-524.08, 761.4) * mm, v(-519.3, 789.29) * mm]});
            skFitSpline(sketch, "E579", {"points": [v(-519.3, 789.29) * mm, v(-508.52, 852.2) * mm, v(-467.76, 885.05) * mm, v(-399.4, 885.9) * mm]});
            skFitSpline(sketch, "E580", {"points": [v(-399.4, 885.9) * mm, v(-332.27, 886.75) * mm, v(-294.76, 845.83) * mm, v(-279.04, 754.6) * mm]});
            skFitSpline(sketch, "E581", {"points": [v(-279.04, 754.6) * mm, v(-276.27, 738.54) * mm, v(-277.28, 735.94) * mm, v(-287.34, 733.25) * mm]});
            skFitSpline(sketch, "E582", {"points": [v(-287.34, 733.25) * mm, v(-307.7, 727.8) * mm, v(-309.53, 729.59) * mm, v(-315.3, 760.66) * mm]});
            skFitSpline(sketch, "E583", {"points": [v(-315.3, 760.66) * mm, v(-322.94, 801.69) * mm, v(-335.5, 825.75) * mm, v(-356.75, 840.09) * mm]});
            skFitSpline(sketch, "E584", {"points": [v(-356.75, 840.09) * mm, v(-372.12, 850.45) * mm, v(-378.77, 851.69) * mm, v(-408.26, 849.66) * mm]});
            skFitSpline(sketch, "E585", {"points": [v(-408.26, 849.66) * mm, v(-462.47, 845.94) * mm, v(-481.98, 825.59) * mm, v(-486.47, 768.07) * mm]});
            skFitSpline(sketch, "E586", {"points": [v(-486.47, 768.07) * mm, v(-489.35, 731.13) * mm, v(-460.61, 464.93) * mm, v(-449.81, 428.56) * mm]});
            skFitSpline(sketch, "E587", {"points": [v(-449.81, 428.56) * mm, v(-440, 395.5) * mm, v(-422.85, 375.46) * mm, v(-398.05, 368.03) * mm]});
            skFitSpline(sketch, "E588", {"points": [v(-398.05, 368.03) * mm, v(-373.87, 360.78) * mm, v(-364.61, 360.67) * mm, v(-340.58, 367.35) * mm]});
            skFitSpline(sketch, "E589", {"points": [v(-340.58, 367.35) * mm, v(-294.31, 380.2) * mm, v(-276.32, 427.15) * mm, v(-286.51, 508.44) * mm]});
            skFitSpline(sketch, "E590", {"points": [v(-286.51, 508.44) * mm, v(-289.44, 531.78) * mm, v(-292.78, 551.82) * mm, v(-293.94, 552.97) * mm]});
            skFitSpline(sketch, "E591", {"points": [v(-293.94, 552.97) * mm, v(-295.1, 554.13) * mm, v(-318.85, 552.48) * mm, v(-346.74, 549.31) * mm]});
            skFitSpline(sketch, "E592", {"points": [v(-346.74, 549.31) * mm, v(-415.73, 541.47) * mm, v(-412.2, 540.86) * mm, v(-412.2, 560.5) * mm]});
            skFitSpline(sketch, "E593", {"points": [v(-358.01, 583.3) * mm, v(-328.21, 586.52) * mm, v(-294.48, 590.45) * mm, v(-283.05, 592.03) * mm]});
            skFitSpline(sketch, "E594", {"points": [v(-283.05, 592.03) * mm, v(-262.7, 594.85) * mm, v(-262.21, 594.56) * mm, v(-259.28, 578.05) * mm]});
            skFitSpline(sketch, "E595", {"points": [v(-259.28, 578.05) * mm, v(-257.64, 568.78) * mm, v(-254.74, 530.1) * mm, v(-252.84, 492.1) * mm]});
            skFitSpline(sketch, "E596", {"points": [v(-252.84, 492.1) * mm, v(-249.91, 433.68) * mm, v(-250.68, 419.66) * mm, v(-257.84, 401.37) * mm]});
            skFitSpline(sketch, "E597", {"points": [v(-257.84, 401.37) * mm, v(-272.96, 362.7) * mm, v(-301.8, 339.73) * mm, v(-342.1, 334.25) * mm]});
            skFitSpline(sketch, "E598", {"points": [v(-342.1, 334.25) * mm, v(-354.32, 332.58) * mm, v(-368.85, 330.55) * mm, v(-374.4, 329.73) * mm]});
            skFitSpline(sketch, "E599", {"points": [v(-374.4, 329.73) * mm, v(-379.94, 328.9) * mm, v(-389.01, 329.16) * mm, v(-394.56, 330.28) * mm]});
            skFitSpline(sketch, "E600", {"points": [v(377.09, 345.72) * mm, v(375.48, 356.11) * mm, v(370.5, 394.1) * mm, v(366.03, 430.14) * mm]});
            skFitSpline(sketch, "E601", {"points": [v(366.03, 430.14) * mm, v(361.56, 466.18) * mm, v(357.25, 496.37) * mm, v(356.44, 497.24) * mm]});
            skFitSpline(sketch, "E602", {"points": [v(356.44, 497.24) * mm, v(354.96, 498.84) * mm, v(220.95, 512.8) * mm, v(219.65, 511.5) * mm]});
            skFitSpline(sketch, "E603", {"points": [v(219.65, 511.5) * mm, v(219.26, 511.1) * mm, v(207.17, 473.68) * mm, v(192.8, 428.33) * mm]});
            skFitSpline(sketch, "E604", {"points": [v(151.03, 349) * mm, v(142.44, 350.72) * mm, v(134.45, 353.08) * mm, v(133.27, 354.26) * mm]});
            skFitSpline(sketch, "E605", {"points": [v(133.27, 354.26) * mm, v(132.1, 355.44) * mm, v(171.6, 477.9) * mm, v(221.07, 626.39) * mm]});
            skFitSpline(sketch, "E606", {"points": [v(221.07, 626.39) * mm, v(310.4, 894.52) * mm, v(311.11, 896.37) * mm, v(324.68, 896.37) * mm]});
            skFitSpline(sketch, "E607", {"points": [v(324.68, 896.37) * mm, v(341.4, 896.37) * mm, v(335.84, 927.07) * mm, v(376.61, 609.07) * mm]});
            skFitSpline(sketch, "E608", {"points": [v(376.61, 609.07) * mm, v(394.56, 469.08) * mm, v(410.35, 348.3) * mm, v(411.7, 340.68) * mm]});
            skFitSpline(sketch, "E609", {"points": [v(411.7, 340.68) * mm, v(413.99, 327.8) * mm, v(412.95, 326.82) * mm, v(397.09, 326.82) * mm]});
            skFitSpline(sketch, "E610", {"points": [v(397.09, 326.82) * mm, v(381.24, 326.82) * mm, v(379.8, 328.17) * mm, v(377.09, 345.72) * mm]});
            skFitSpline(sketch, "E611", {"points": [v(349.8, 553.78) * mm, v(346.64, 588.07) * mm, v(318.17, 792.68) * mm, v(316.3, 794.56) * mm]});
            skFitSpline(sketch, "E612", {"points": [v(316.3, 794.56) * mm, v(315.25, 795.6) * mm, v(297.03, 742.72) * mm, v(275.83, 677.02) * mm]});
            skFitSpline(sketch, "E613", {"points": [v(275.83, 677.02) * mm, v(254.62, 611.33) * mm, v(236.15, 554.68) * mm, v(234.8, 551.13) * mm]});
            skFitSpline(sketch, "E614", {"points": [v(234.8, 551.13) * mm, v(232.95, 546.33) * mm, v(245.58, 543.43) * mm, v(284.3, 539.77) * mm]});
            skFitSpline(sketch, "E615", {"points": [v(284.3, 539.77) * mm, v(353.48, 533.23) * mm, v(351.73, 532.85) * mm, v(349.8, 553.78) * mm]});
            skFitSpline(sketch, "E616", {"points": [v(-171.95, 546.96) * mm, v(-173.79, 657.36) * mm, v(-175.3, 784.54) * mm, v(-175.3, 829.59) * mm]});
            skFitSpline(sketch, "E617", {"points": [v(-103.48, 911.46) * mm, v(-24.03, 911.43) * mm, v(-0.34, 906.93) * mm, v(24.87, 887.07) * mm]});
            skFitSpline(sketch, "E618", {"points": [v(24.87, 887.07) * mm, v(58.1, 860.91) * mm, v(76.2, 788.6) * mm, v(65.97, 722.92) * mm]});
            skFitSpline(sketch, "E619", {"points": [v(65.97, 722.92) * mm, v(58.62, 675.7) * mm, v(49.61, 656.77) * mm, v(26.51, 640.04) * mm]});
            skFitSpline(sketch, "E620", {"points": [v(25.48, 607.36) * mm, v(57.67, 575.93) * mm, v(63.07, 554.21) * mm, v(65.47, 446.52) * mm]});
            skFitSpline(sketch, "E621", {"points": [v(31.35, 437.53) * mm, v(31.35, 532.63) * mm, v(25.57, 560.99) * mm, v(1.97, 581.77) * mm]});
            skFitSpline(sketch, "E622", {"points": [v(1.97, 581.77) * mm, v(-19.72, 600.87) * mm, v(-53.3, 609.7) * mm, v(-97.89, 608.03) * mm]});
            skFitSpline(sketch, "E623", {"points": [v(-135.57, 479.28) * mm, v(-133.96, 373.36) * mm, v(-134.8, 352) * mm, v(-140.6, 351.95) * mm]});
            skFitSpline(sketch, "E624", {"points": [v(-140.6, 351.95) * mm, v(-144.44, 351.9) * mm, v(-152.31, 350.6) * mm, v(-158.1, 349.06) * mm]});
            skFitSpline(sketch, "E625", {"points": [v(-158.1, 349.06) * mm, v(-168.59, 346.24) * mm, v(-168.62, 346.7) * mm, v(-171.95, 546.96) * mm]});
            skFitSpline(sketch, "E626", {"points": [v(-8.97, 657.1) * mm, v(1.43, 663.1) * mm, v(13.43, 676.53) * mm, v(20.27, 689.83) * mm]});
            skFitSpline(sketch, "E627", {"points": [v(20.27, 689.83) * mm, v(30.76, 710.25) * mm, v(31.72, 718.02) * mm, v(30.35, 771.27) * mm]});
            skFitSpline(sketch, "E628", {"points": [v(30.35, 771.27) * mm, v(28.04, 860.8) * mm, v(15.9, 872.17) * mm, v(-80.8, 875.33) * mm]});
            skFitSpline(sketch, "E629", {"points": [v(-83.32, 645.1) * mm, v(-37.92, 646.56) * mm, v(-23.1, 648.95) * mm, v(-8.97, 657.1) * mm]});
            skSolve(sketch);
        }
        {
            var Q0;
            Q0=qCreatedBy(makeId("Top.planeOp"),FACE);
            var sketch = newSketch(context, id + "F1", { "sketchPlane" : qUnion([Q0])});
            skFitSpline(sketch, "E630.0", {"points": [v(338.8, 1076.26) * mm, v(1177.61, 1009.38) * mm, v(1835.7, 747.59) * mm, v(2121.4, 367.14) * mm]});
            skFitSpline(sketch, "E631.0", {"points": [v(2121.4, 367.14) * mm, v(2251.55, 193.84) * mm, v(2286.19, 7.97) * mm, v(2223.32, -179.71) * mm]});
            skFitSpline(sketch, "E632.0", {"points": [v(2223.32, -179.71) * mm, v(2179.67, -310.03) * mm, v(2067.7, -452.62) * mm, v(1913.9, -573.78) * mm]});
            skFitSpline(sketch, "E633.0", {"points": [v(1913.9, -573.78) * mm, v(1736.48, -713.56) * mm, v(1454.38, -846.93) * mm, v(1154.15, -932.98) * mm]});
            skFitSpline(sketch, "E634.0", {"points": [v(1154.15, -932.98) * mm, v(763.99, -1044.82) * mm, v(330.04, -1095.5) * mm, v(-137.5, -1083.85) * mm]});
            skFitSpline(sketch, "E635.0", {"points": [v(-137.5, -1083.85) * mm, v(-1015.8, -1061.97) * mm, v(-1795.97, -784.8) * mm, v(-2107.84, -383.87) * mm]});
            skFitSpline(sketch, "E636.0", {"points": [v(-2107.84, -383.87) * mm, v(-2158.8, -318.36) * mm, v(-2179.7, -283.92) * mm, v(-2205.75, -222.58) * mm]});
            skFitSpline(sketch, "E637.0", {"points": [v(-2205.75, -222.58) * mm, v(-2267.88, -76.26) * mm, v(-2269.76, 70.75) * mm, v(-2211.35, 214.41) * mm]});
            skFitSpline(sketch, "E638.0", {"points": [v(-2211.35, 214.41) * mm, v(-2147.67, 371.03) * mm, v(-2000.3, 528.9) * mm, v(-1798.84, 656.33) * mm]});
            skFitSpline(sketch, "E639.0", {"points": [v(-1798.84, 656.33) * mm, v(-1440.14, 883.22) * mm, v(-932.63, 1028.95) * mm, v(-336.6, 1076.21) * mm]});
            skFitSpline(sketch, "E640.0", {"points": [v(-336.6, 1076.21) * mm, v(-184.04, 1088.31) * mm, v(187.36, 1088.34) * mm, v(338.8, 1076.26) * mm]});
            skSolve(sketch);
        }
        {
            var Q0;
            Q0=makeQuery(id+"F1.imprint","IMPRINT",FACE,{"disambiguationData":[TD([[makeQuery(id+"F1.imprint","IMPRINT",EDGE,{"derivedFrom":sQuery(id+"F1.wireOp",EDGE,"E630.0")}),-1.0]])]});
            extrude(context, id + "F2", {"entities" : qUnion([Q0]), "oppositeDirection" : true, "depth" : 25.4 * mm, "offsetDistance" : 25.4 * mm});
        }
    });
